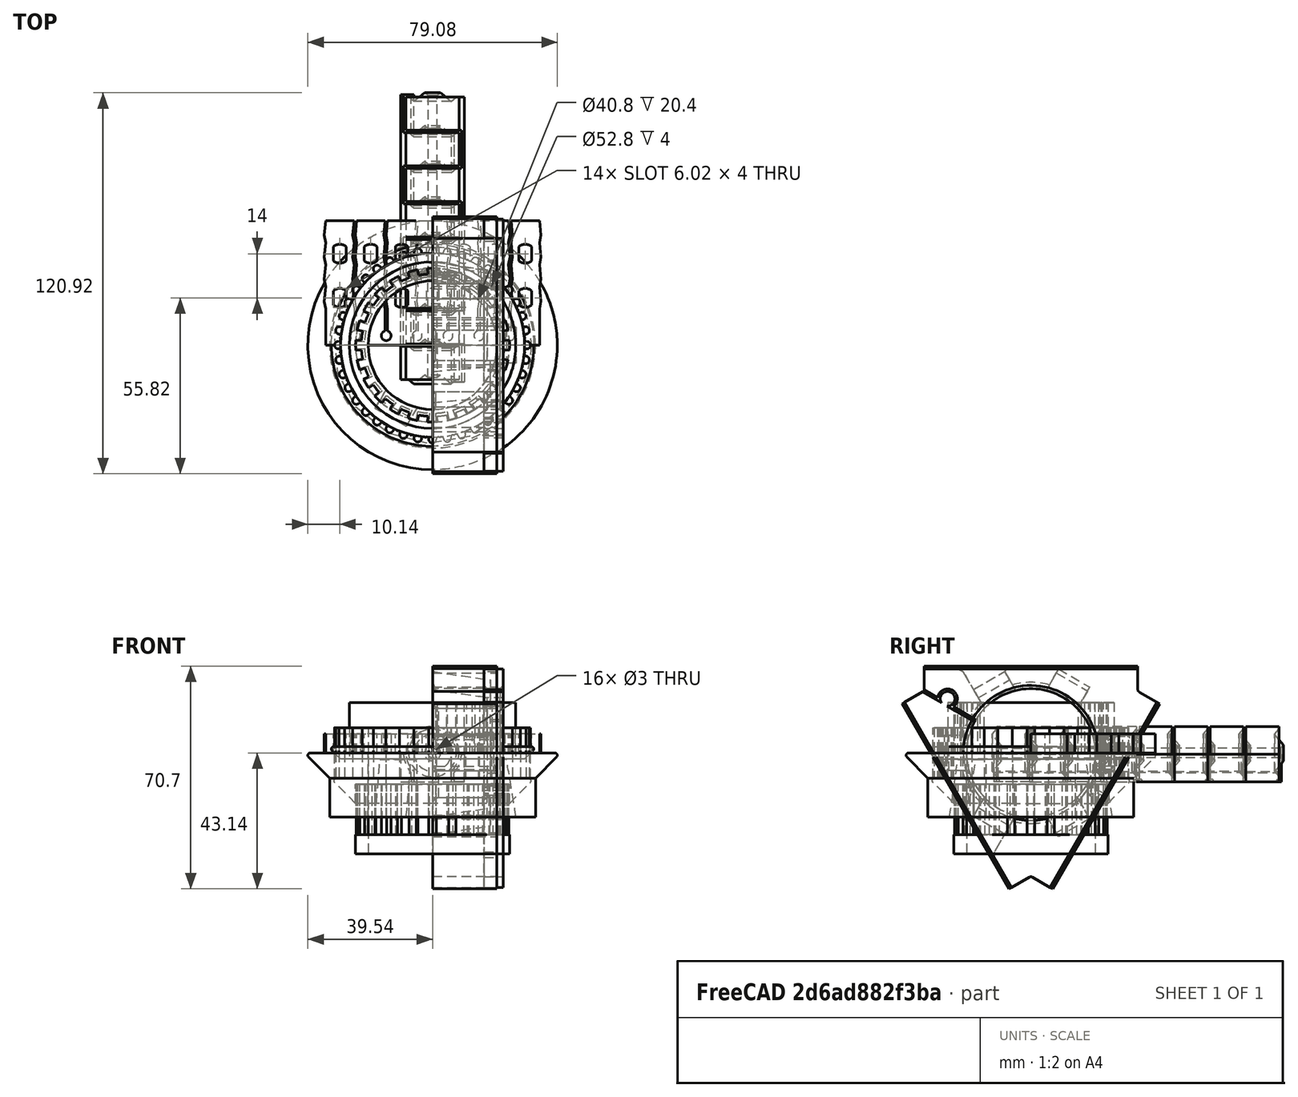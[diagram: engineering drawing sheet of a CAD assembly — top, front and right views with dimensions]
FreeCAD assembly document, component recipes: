
FREECAD ASSEMBLY — COMPONENT RECIPES ("BaseHingeModel_ver1.2_Base")

This assembly document has 10 components, labeled P0..P9 below (a component is one placed body or linked part). 10 of them carry a construction recipe — the FreeCAD feature program that regenerates the part from scratch, quoted from this document or its linked companion documents; the rest are supplied as boundary geometry only. No exploded tour is included for this assembly.
COMPONENT P0 — recipe-attached ("BeamFixatoPart", modeled in this document).
Construction recipe (the document's own serialized feature program — sketch geometry with constraints, then the solid features built on it; lengths are millimeters unless a unit is written):

FEATURE [Sketcher::SketchObject] Sketch022  label="FixatorBodySketch"
  FullyConstrained = false
  MapMode = 5
  Support = -> [XY_Plane005]
  expr: Constraints[143] = Spreadsheet.mmCellWall
  expr: Constraints[144] = Spreadsheet.mmCellWall
  expr: Constraints[145] = Spreadsheet.mmCellWall
  expr: Constraints[146] = Spreadsheet.mmCellWidth
  expr: Constraints[147] = Spreadsheet.mmCellWidth
  expr: Constraints[148] = Spreadsheet.mmCellWidth
  expr: Constraints[169] = Spreadsheet.mmCommonBaseLenght
  expr: Constraints[170] = Spreadsheet.mmToothStep
  expr: Constraints[171] = Spreadsheet.mmToothStep
  expr: Constraints[172] = Spreadsheet.mmToothStep
  expr: Constraints[173] = Spreadsheet.mmToothStep
  expr: Constraints[174] = Spreadsheet.mmToothStep
  expr: Constraints[183] = Spreadsheet.mmCellWall * 3
  expr: Constraints[184] = Spreadsheet.mmCellWall * 3
  expr: Constraints[185] = Spreadsheet.mmCellWall * 3
  expr: Constraints[186] = Spreadsheet.mmCellWall * 3
  expr: Constraints[425] = Spreadsheet.mmFirstCircleArcToBase
  expr: Constraints[435] = Spreadsheet.mmCellWall / 2
  expr: Constraints[464] = Spreadsheet.mmCellWidth + Spreadsheet.mmCellWall
  expr: Constraints[5] = Spreadsheet.mmBaseWidth
  expr: Constraints[6] = Spreadsheet.mmBaseEnd
  sketch-geometry (155):
    g0: LineSegment StartX=-33.9 StartY=0 StartZ=0 EndX=-33.9 EndY=39.5 EndZ=0
    g1: LineSegment StartX=-33.9 StartY=39.5 StartZ=0 EndX=33.9 EndY=39.5 EndZ=0
    g2: LineSegment StartX=33.9 StartY=39.5 StartZ=0 EndX=33.9 EndY=0 EndZ=0
    g3: LineSegment StartX=-73.1099 StartY=25.5 StartZ=0 EndX=65.6354 EndY=25.5 EndZ=0
    g4: LineSegment StartX=-33.9 StartY=0 StartZ=0 EndX=-33.9 EndY=11.5 EndZ=0
    g5: LineSegment StartX=-33.9 StartY=11.5 StartZ=0 EndX=-34.3 EndY=13.9 EndZ=0
    g6: LineSegment StartX=-34.3 StartY=13.9 StartZ=0 EndX=-33.9 EndY=18.5 EndZ=0
    g7: LineSegment StartX=-33.9 StartY=18.5 StartZ=0 EndX=-34.3 EndY=20.9 EndZ=0
    g8: LineSegment StartX=-34.3 StartY=20.9 StartZ=0 EndX=-33.9 EndY=25.5 EndZ=0
    g9: LineSegment StartX=-33.9 StartY=25.5 StartZ=0 EndX=-34.3 EndY=27.9 EndZ=0
    g10: LineSegment StartX=-34.3 StartY=27.9 StartZ=0 EndX=-33.9 EndY=32.5 EndZ=0
    g11: LineSegment StartX=-33.9 StartY=32.5 StartZ=0 EndX=-34.3 EndY=34.9 EndZ=0
    g12: LineSegment StartX=-34.3 StartY=34.9 StartZ=0 EndX=-33.9 EndY=39.5 EndZ=0
    g13: LineSegment StartX=-33.9 StartY=39.5 StartZ=0 EndX=-24.9 EndY=39.5 EndZ=0
    g14: LineSegment StartX=-24.9 StartY=39.5 StartZ=0 EndX=-25.3 EndY=34.9 EndZ=0
    g15: LineSegment StartX=-25.3 StartY=34.9 StartZ=0 EndX=-24.9 EndY=32.5 EndZ=0
    g16: LineSegment StartX=-24.9 StartY=32.5 StartZ=0 EndX=-25.3 EndY=27.9 EndZ=0
    g17: LineSegment StartX=-25.3 StartY=27.9 StartZ=0 EndX=-24.9 EndY=25.5 EndZ=0
    g18: LineSegment StartX=-24.9 StartY=25.5 StartZ=0 EndX=-25.3 EndY=20.9 EndZ=0
    g19: LineSegment StartX=-25.3 StartY=20.9 StartZ=0 EndX=-24.9 EndY=18.5 EndZ=0
    g20: LineSegment StartX=-24.9 StartY=18.5 StartZ=0 EndX=-25.3 EndY=13.9 EndZ=0
    g21: LineSegment StartX=-25.3 StartY=13.9 StartZ=0 EndX=-24.9 EndY=11.5 EndZ=0
    g22: LineSegment StartX=-24.9 StartY=11.5 StartZ=0 EndX=-24.9 EndY=4.5 EndZ=0
    g23: LineSegment StartX=-24.1 StartY=4.5 StartZ=0 EndX=-24.1 EndY=11.5 EndZ=0
    g24: LineSegment StartX=-24.1 StartY=11.5 StartZ=0 EndX=-24.5 EndY=13.9 EndZ=0
    g25: LineSegment StartX=-24.5 StartY=13.9 StartZ=0 EndX=-24.1 EndY=18.5 EndZ=0
    g26: LineSegment StartX=-24.1 StartY=18.5 StartZ=0 EndX=-24.5 EndY=20.9 EndZ=0
    g27: LineSegment StartX=-24.5 StartY=20.9 StartZ=0 EndX=-24.1 EndY=25.5 EndZ=0
    g28: LineSegment StartX=-24.1 StartY=25.5 StartZ=0 EndX=-24.5 EndY=27.9 EndZ=0
    g29: LineSegment StartX=-24.5 StartY=27.9 StartZ=0 EndX=-24.1 EndY=32.5 EndZ=0
    g30: LineSegment StartX=-24.1 StartY=32.5 StartZ=0 EndX=-24.5 EndY=34.9 EndZ=0
    g31: LineSegment StartX=-24.5 StartY=34.9 StartZ=0 EndX=-24.1 EndY=39.5 EndZ=0
    g32: LineSegment StartX=-24.1 StartY=39.5 StartZ=0 EndX=-15.1 EndY=39.5 EndZ=0
    g33: LineSegment StartX=-15.1 StartY=39.5 StartZ=0 EndX=-15.5 EndY=34.9 EndZ=0
    g34: LineSegment StartX=-15.5 StartY=34.9 StartZ=0 EndX=-15.1 EndY=32.5 EndZ=0
    g35: LineSegment StartX=-15.1 StartY=32.5 StartZ=0 EndX=-15.5 EndY=27.9 EndZ=0
    g36: LineSegment StartX=-15.5 StartY=27.9 StartZ=0 EndX=-15.1 EndY=25.5 EndZ=0
    g37: LineSegment StartX=-15.1 StartY=25.5 StartZ=0 EndX=-15.5 EndY=20.9 EndZ=0
    g38: LineSegment StartX=-15.5 StartY=20.9 StartZ=0 EndX=-15.1 EndY=18.5 EndZ=0
    g39: LineSegment StartX=-15.1 StartY=18.5 StartZ=0 EndX=-15.5 EndY=13.9 EndZ=0
    g40: LineSegment StartX=-15.5 StartY=13.9 StartZ=0 EndX=-15.1 EndY=11.5 EndZ=0
    g41: LineSegment StartX=-15.1 StartY=11.5 StartZ=0 EndX=-15.1 EndY=4.5 EndZ=0
    g42: LineSegment StartX=-14.3 StartY=4.5 StartZ=0 EndX=-14.3 EndY=11.5 EndZ=0
    g43: LineSegment StartX=-14.3 StartY=11.5 StartZ=0 EndX=-14.7 EndY=13.9 EndZ=0
    g44: LineSegment StartX=-14.7 StartY=13.9 StartZ=0 EndX=-14.3 EndY=18.5 EndZ=0
    g45: LineSegment StartX=-14.3 StartY=18.5 StartZ=0 EndX=-14.7 EndY=20.9 EndZ=0
    g46: LineSegment StartX=-14.7 StartY=20.9 StartZ=0 EndX=-14.3 EndY=25.5 EndZ=0
    g47: LineSegment StartX=-14.3 StartY=25.5 StartZ=0 EndX=-14.7 EndY=27.9 EndZ=0
    g48: LineSegment StartX=-14.7 StartY=27.9 StartZ=0 EndX=-14.3 EndY=32.5 EndZ=0
    g49: LineSegment StartX=-14.3 StartY=32.5 StartZ=0 EndX=-14.7 EndY=34.9 EndZ=0
    g50: LineSegment StartX=-14.7 StartY=34.9 StartZ=0 EndX=-14.3 EndY=39.5 EndZ=0
    g51: LineSegment StartX=-14.3 StartY=39.5 StartZ=0 EndX=-5.3 EndY=39.5 EndZ=0
    g52: LineSegment StartX=-5.3 StartY=39.5 StartZ=0 EndX=-5.7 EndY=34.9 EndZ=0
    g53: LineSegment StartX=-5.7 StartY=34.9 StartZ=0 EndX=-5.3 EndY=32.5 EndZ=0
    g54: LineSegment StartX=-5.3 StartY=32.5 StartZ=0 EndX=-5.7 EndY=27.9 EndZ=0
    g55: LineSegment StartX=-5.7 StartY=27.9 StartZ=0 EndX=-5.3 EndY=25.5 EndZ=0
    g56: LineSegment StartX=-5.3 StartY=25.5 StartZ=0 EndX=-5.7 EndY=20.9 EndZ=0
    g57: LineSegment StartX=-5.7 StartY=20.9 StartZ=0 EndX=-5.3 EndY=18.5 EndZ=0
    g58: LineSegment StartX=-5.3 StartY=18.5 StartZ=0 EndX=-5.7 EndY=13.9 EndZ=0
    g59: LineSegment StartX=-5.7 StartY=13.9 StartZ=0 EndX=-5.3 EndY=11.5 EndZ=0
    g60: LineSegment StartX=-5.3 StartY=11.5 StartZ=0 EndX=-5.3 EndY=4.5 EndZ=0
    g61: LineSegment StartX=-4.5 StartY=4.5 StartZ=0 EndX=-4.5 EndY=11.5 EndZ=0
    g62: LineSegment StartX=-4.5 StartY=11.5 StartZ=0 EndX=-4.9 EndY=13.9 EndZ=0
    g63: LineSegment StartX=-4.9 StartY=13.9 StartZ=0 EndX=-4.5 EndY=18.5 EndZ=0
    g64: LineSegment StartX=-4.5 StartY=18.5 StartZ=0 EndX=-4.9 EndY=20.9 EndZ=0
    g65: LineSegment StartX=-4.9 StartY=20.9 StartZ=0 EndX=-4.5 EndY=25.5 EndZ=0
    g66: LineSegment StartX=-4.5 StartY=25.5 StartZ=0 EndX=-4.9 EndY=27.9 EndZ=0
    g67: LineSegment StartX=-4.9 StartY=27.9 StartZ=0 EndX=-4.5 EndY=32.5 EndZ=0
    g68: LineSegment StartX=-4.5 StartY=32.5 StartZ=0 EndX=-4.9 EndY=34.9 EndZ=0
    g69: LineSegment StartX=-4.9 StartY=34.9 StartZ=0 EndX=-4.5 EndY=39.5 EndZ=0
    g70: LineSegment StartX=-4.5 StartY=39.5 StartZ=0 EndX=4.5 EndY=39.5 EndZ=0
    g71: LineSegment StartX=4.5 StartY=39.5 StartZ=0 EndX=4.9 EndY=34.9 EndZ=0
    g72: LineSegment StartX=4.9 StartY=34.9 StartZ=0 EndX=4.5 EndY=32.5 EndZ=0
    g73: LineSegment StartX=4.5 StartY=32.5 StartZ=0 EndX=4.9 EndY=27.9 EndZ=0
    g74: LineSegment StartX=4.9 StartY=27.9 StartZ=0 EndX=4.5 EndY=25.5 EndZ=0
    g75: LineSegment StartX=4.5 StartY=25.5 StartZ=0 EndX=4.9 EndY=20.9 EndZ=0
    g76: LineSegment StartX=4.9 StartY=20.9 StartZ=0 EndX=4.5 EndY=18.5 EndZ=0
    g77: LineSegment StartX=4.5 StartY=18.5 StartZ=0 EndX=4.9 EndY=13.9 EndZ=0
    g78: LineSegment StartX=4.9 StartY=13.9 StartZ=0 EndX=4.5 EndY=11.5 EndZ=0
    g79: LineSegment StartX=4.5 StartY=11.5 StartZ=0 EndX=4.5 EndY=4.5 EndZ=0
    g80: LineSegment StartX=5.3 StartY=4.5 StartZ=0 EndX=5.3 EndY=11.5 EndZ=0
    g81: LineSegment StartX=5.3 StartY=11.5 StartZ=0 EndX=5.7 EndY=13.9 EndZ=0
    g82: LineSegment StartX=5.7 StartY=13.9 StartZ=0 EndX=5.3 EndY=18.5 EndZ=0
    g83: LineSegment StartX=5.3 StartY=18.5 StartZ=0 EndX=5.7 EndY=20.9 EndZ=0
    g84: LineSegment StartX=5.7 StartY=20.9 StartZ=0 EndX=5.3 EndY=25.5 EndZ=0
    g85: LineSegment StartX=5.3 StartY=25.5 StartZ=0 EndX=5.7 EndY=27.9 EndZ=0
    g86: LineSegment StartX=5.7 StartY=27.9 StartZ=0 EndX=5.3 EndY=32.5 EndZ=0
    g87: LineSegment StartX=5.3 StartY=32.5 StartZ=0 EndX=5.7 EndY=34.9 EndZ=0
    g88: LineSegment StartX=5.7 StartY=34.9 StartZ=0 EndX=5.3 EndY=39.5 EndZ=0
    g89: LineSegment StartX=5.3 StartY=39.5 StartZ=0 EndX=14.3 EndY=39.5 EndZ=0
    g90: LineSegment StartX=14.3 StartY=39.5 StartZ=0 EndX=14.7 EndY=34.9 EndZ=0
    g91: LineSegment StartX=14.7 StartY=34.9 StartZ=0 EndX=14.3 EndY=32.5 EndZ=0
    g92: LineSegment StartX=14.3 StartY=32.5 StartZ=0 EndX=14.7 EndY=27.9 EndZ=0
    g93: LineSegment StartX=14.7 StartY=27.9 StartZ=0 EndX=14.3 EndY=25.5 EndZ=0
    g94: LineSegment StartX=14.3 StartY=25.5 StartZ=0 EndX=14.7 EndY=20.9 EndZ=0
    g95: LineSegment StartX=14.7 StartY=20.9 StartZ=0 EndX=14.3 EndY=18.5 EndZ=0
    g96: LineSegment StartX=14.3 StartY=18.5 StartZ=0 EndX=14.7 EndY=13.9 EndZ=0
    g97: LineSegment StartX=14.7 StartY=13.9 StartZ=0 EndX=14.3 EndY=11.5 EndZ=0
    g98: LineSegment StartX=14.3 StartY=11.5 StartZ=0 EndX=14.3 EndY=4.5 EndZ=0
    g99: LineSegment StartX=15.1 StartY=4.5 StartZ=0 EndX=15.1 EndY=11.5 EndZ=0
    g100: LineSegment StartX=15.1 StartY=11.5 StartZ=0 EndX=15.5 EndY=13.9 EndZ=0
    g101: LineSegment StartX=15.5 StartY=13.9 StartZ=0 EndX=15.1 EndY=18.5 EndZ=0
    g102: LineSegment StartX=15.1 StartY=18.5 StartZ=0 EndX=15.5 EndY=20.9 EndZ=0
    g103: LineSegment StartX=15.5 StartY=20.9 StartZ=0 EndX=15.1 EndY=25.5 EndZ=0
    g104: LineSegment StartX=15.1 StartY=25.5 StartZ=0 EndX=15.5 EndY=27.9 EndZ=0
    g105: LineSegment StartX=15.5 StartY=27.9 StartZ=0 EndX=15.1 EndY=32.5 EndZ=0
    g106: LineSegment StartX=15.1 StartY=32.5 StartZ=0 EndX=15.5 EndY=34.9 EndZ=0
    g107: LineSegment StartX=15.5 StartY=34.9 StartZ=0 EndX=15.1 EndY=39.5 EndZ=0
    g108: LineSegment StartX=15.1 StartY=39.5 StartZ=0 EndX=24.1 EndY=39.5 EndZ=0
    g109: LineSegment StartX=24.1 StartY=39.5 StartZ=0 EndX=24.5 EndY=34.9 EndZ=0
    g110: LineSegment StartX=24.5 StartY=34.9 StartZ=0 EndX=24.1 EndY=32.5 EndZ=0
    g111: LineSegment StartX=24.1 StartY=32.5 StartZ=0 EndX=24.5 EndY=27.9 EndZ=0
    g112: LineSegment StartX=24.5 StartY=27.9 StartZ=0 EndX=24.1 EndY=25.5 EndZ=0
    g113: LineSegment StartX=24.1 StartY=25.5 StartZ=0 EndX=24.5 EndY=20.9 EndZ=0
    g114: LineSegment StartX=24.5 StartY=20.9 StartZ=0 EndX=24.1 EndY=18.5 EndZ=0
    g115: LineSegment StartX=24.1 StartY=18.5 StartZ=0 EndX=24.5 EndY=13.9 EndZ=0
    g116: LineSegment StartX=24.5 StartY=13.9 StartZ=0 EndX=24.1 EndY=11.5 EndZ=0
    g117: LineSegment StartX=24.1 StartY=11.5 StartZ=0 EndX=24.1 EndY=4.5 EndZ=0
    g118: LineSegment StartX=24.9 StartY=4.5 StartZ=0 EndX=24.9 EndY=11.5 EndZ=0
    g119: LineSegment StartX=24.9 StartY=11.5 StartZ=0 EndX=25.3 EndY=13.9 EndZ=0
    g120: LineSegment StartX=25.3 StartY=13.9 StartZ=0 EndX=24.9 EndY=18.5 EndZ=0
    g121: LineSegment StartX=24.9 StartY=18.5 StartZ=0 EndX=25.3 EndY=20.9 EndZ=0
    g122: LineSegment StartX=25.3 StartY=20.9 StartZ=0 EndX=24.9 EndY=25.5 EndZ=0
    g123: LineSegment StartX=24.9 StartY=25.5 StartZ=0 EndX=25.3 EndY=27.9 EndZ=0
    g124: LineSegment StartX=25.3 StartY=27.9 StartZ=0 EndX=24.9 EndY=32.5 EndZ=0
    g125: LineSegment StartX=24.9 StartY=32.5 StartZ=0 EndX=25.3 EndY=34.9 EndZ=0
    g126: LineSegment StartX=25.3 StartY=34.9 StartZ=0 EndX=24.9 EndY=39.5 EndZ=0
    g127: LineSegment StartX=24.9 StartY=39.5 StartZ=0 EndX=33.9 EndY=39.5 EndZ=0
    g128: LineSegment StartX=33.9 StartY=39.5 StartZ=0 EndX=34.3 EndY=34.9 EndZ=0
    g129: LineSegment StartX=34.3 StartY=34.9 StartZ=0 EndX=33.9 EndY=32.5 EndZ=0
    g130: LineSegment StartX=33.9 StartY=32.5 StartZ=0 EndX=34.3 EndY=27.9 EndZ=0
    g131: LineSegment StartX=34.3 StartY=27.9 StartZ=0 EndX=33.9 EndY=25.5 EndZ=0
    g132: LineSegment StartX=33.9 StartY=25.5 StartZ=0 EndX=34.3 EndY=20.9 EndZ=0
    g133: LineSegment StartX=34.3 StartY=20.9 StartZ=0 EndX=33.9 EndY=18.5 EndZ=0
    g134: LineSegment StartX=33.9 StartY=18.5 StartZ=0 EndX=34.3 EndY=13.9 EndZ=0
    g135: LineSegment StartX=34.3 StartY=13.9 StartZ=0 EndX=33.9 EndY=11.5 EndZ=0
    g136: LineSegment StartX=33.9 StartY=11.5 StartZ=0 EndX=33.9 EndY=0 EndZ=0
    g137: LineSegment StartX=33.9 StartY=0 StartZ=0 EndX=-33.9 EndY=0 EndZ=0
    g138: LineSegment StartX=-73.1099 StartY=18.5 StartZ=0 EndX=65.6354 EndY=18.5 EndZ=0
    g139: LineSegment StartX=-73.1099 StartY=34.9 StartZ=0 EndX=65.6354 EndY=34.9 EndZ=0
    g140: LineSegment StartX=-73.1099 StartY=32.5 StartZ=0 EndX=65.6354 EndY=32.5 EndZ=0
    g141: LineSegment StartX=-73.1099 StartY=27.9 StartZ=0 EndX=65.6354 EndY=27.9 EndZ=0
    g142: LineSegment StartX=-73.1099 StartY=20.9 StartZ=0 EndX=65.6354 EndY=20.9 EndZ=0
    g143: LineSegment StartX=-73.1099 StartY=11.5 StartZ=0 EndX=65.6354 EndY=11.5 EndZ=0
    g144: LineSegment StartX=-34.3 StartY=8.59208 StartZ=0 EndX=-34.3 EndY=49.4346 EndZ=0
    g145: LineSegment StartX=-73.1099 StartY=13.9 StartZ=0 EndX=65.6354 EndY=13.9 EndZ=0
    g146: LineSegment StartX=-33.9 StartY=0 StartZ=0 EndX=33.9 EndY=0 EndZ=0
    g147: LineSegment StartX=-73.1099 StartY=4.5 StartZ=0 EndX=65.6354 EndY=4.5 EndZ=0
    g148: ArcOfCircle CenterX=-24.5 CenterY=3 CenterZ=0 NormalX=0 NormalY=0 NormalZ=1 AngleXU=0 Radius=1.55242 StartAngle=1.8314 EndAngle=7.59338
    g149: ArcOfCircle CenterX=-14.7 CenterY=3 CenterZ=0 NormalX=0 NormalY=0 NormalZ=1 AngleXU=0 Radius=1.55242 StartAngle=1.8314 EndAngle=7.59338
    g150: ArcOfCircle CenterX=-4.9 CenterY=3 CenterZ=0 NormalX=0 NormalY=0 NormalZ=1 AngleXU=0 Radius=1.55242 StartAngle=1.8314 EndAngle=7.59338
    g151: ArcOfCircle CenterX=4.9 CenterY=3 CenterZ=0 NormalX=0 NormalY=0 NormalZ=1 AngleXU=0 Radius=1.55242 StartAngle=1.8314 EndAngle=7.59338
    g152: ArcOfCircle CenterX=14.7 CenterY=3 CenterZ=0 NormalX=0 NormalY=0 NormalZ=1 AngleXU=0 Radius=1.55242 StartAngle=1.8314 EndAngle=7.59338
    g153: ArcOfCircle CenterX=24.5 CenterY=3 CenterZ=0 NormalX=0 NormalY=0 NormalZ=1 AngleXU=0 Radius=1.55242 StartAngle=1.8314 EndAngle=7.59338
    g154: LineSegment StartX=-73.1099 StartY=3 StartZ=0 EndX=65.6354 EndY=3 EndZ=0
  constraints (469):
    c: Coincident(g0,g1)
    c: Coincident(g1,g2)
    c: Horizontal(g3)
    c: Symmetric(g0,g2,g-2)
    c: Symmetric(g1,g0,g-2)
    c: DistanceX(g0,g2) = 67.8
    c: DistanceX(g0,g1) = 67.8
    c: Coincident(g4,g5)
    c: Coincident(g5,g6)
    c: Coincident(g6,g7)
    c: Coincident(g7,g8)
    c: Coincident(g8,g9)
    c: Coincident(g9,g10)
    c: Coincident(g10,g11)
    c: Coincident(g11,g12)
    c: Coincident(g12,g13)
    c: Horizontal(g13)
    c: Coincident(g13,g14)
    c: Coincident(g14,g15)
    c: Coincident(g15,g16)
    c: Coincident(g16,g17)
    c: Coincident(g17,g18)
    c: Coincident(g18,g19)
    c: Coincident(g19,g20)
    c: Coincident(g20,g21)
    c: Coincident(g21,g22)
    c: Coincident(g23,g24)
    c: Coincident(g24,g25)
    c: Coincident(g25,g26)
    c: Coincident(g26,g27)
    c: Coincident(g27,g28)
    c: Coincident(g28,g29)
    c: Coincident(g29,g30)
    c: Coincident(g30,g31)
    c: Coincident(g31,g32)
    c: Horizontal(g32)
    c: Coincident(g32,g33)
    c: Coincident(g33,g34)
    c: Coincident(g34,g35)
    c: Coincident(g35,g36)
    c: Coincident(g36,g37)
    c: Coincident(g37,g38)
    c: Coincident(g38,g39)
    c: Coincident(g39,g40)
    c: Coincident(g40,g41)
    c: Coincident(g42,g43)
    c: Coincident(g43,g44)
    c: Coincident(g44,g45)
    c: Coincident(g45,g46)
    c: Coincident(g46,g47)
    c: Coincident(g47,g48)
    c: Coincident(g48,g49)
    c: Coincident(g49,g50)
    c: Coincident(g50,g51)
    c: Coincident(g51,g52)
    c: Coincident(g52,g53)
    c: Coincident(g53,g54)
    c: Coincident(g54,g55)
    c: Coincident(g55,g56)
    c: Coincident(g56,g57)
    c: Coincident(g57,g58)
    c: Coincident(g58,g59)
    c: Coincident(g59,g60)
    c: Coincident(g61,g62)
    c: Coincident(g62,g63)
    c: Coincident(g63,g64)
    c: Coincident(g64,g65)
    c: Coincident(g65,g66)
    c: Coincident(g66,g67)
    c: Coincident(g67,g68)
    c: Coincident(g68,g69)
    c: Coincident(g69,g70)
    c: Coincident(g70,g71)
    c: Coincident(g71,g72)
    c: Coincident(g72,g73)
    c: Coincident(g73,g74)
    c: Coincident(g74,g75)
    c: Coincident(g75,g76)
    c: Coincident(g76,g77)
    c: Coincident(g77,g78)
    c: Coincident(g78,g79)
    c: Coincident(g80,g81)
    c: Coincident(g81,g82)
    c: Coincident(g82,g83)
    c: Coincident(g83,g84)
    c: Coincident(g84,g85)
    c: Coincident(g85,g86)
    c: Coincident(g86,g87)
    c: Coincident(g87,g88)
    c: Coincident(g88,g89)
    c: Horizontal(g89)
    c: Coincident(g89,g90)
    c: Coincident(g90,g91)
    c: Coincident(g91,g92)
    c: Coincident(g92,g93)
    c: Coincident(g93,g94)
    c: Coincident(g94,g95)
    c: Coincident(g95,g96)
    c: Coincident(g96,g97)
    c: Coincident(g97,g98)
    c: Coincident(g99,g100)
    c: Coincident(g100,g101)
    c: Coincident(g101,g102)
    c: Coincident(g102,g103)
    c: Coincident(g103,g104)
    c: Coincident(g104,g105)
    c: Coincident(g105,g106)
    c: Coincident(g106,g107)
    c: Coincident(g107,g108)
    c: Coincident(g108,g109)
    c: Coincident(g109,g110)
    c: Coincident(g110,g111)
    c: Coincident(g111,g112)
    c: Coincident(g112,g113)
    c: Coincident(g113,g114)
    c: Coincident(g114,g115)
    c: Coincident(g115,g116)
    c: Coincident(g116,g117)
    c: Coincident(g118,g119)
    c: Coincident(g119,g120)
    c: Coincident(g120,g121)
    c: Coincident(g121,g122)
    c: Coincident(g122,g123)
    c: Coincident(g123,g124)
    c: Coincident(g124,g125)
    c: Coincident(g125,g126)
    c: Coincident(g126,g127)
    c: Coincident(g127,g128)
    c: Coincident(g128,g129)
    c: Coincident(g129,g130)
    c: Coincident(g130,g131)
    c: Coincident(g131,g132)
    c: Coincident(g132,g133)
    c: Coincident(g133,g134)
    c: Coincident(g134,g135)
    c: Coincident(g135,g136)
    c: Symmetric(g69,g70,g-2)
    c: Symmetric(g51,g88,g-2)
    c: Symmetric(g50,g89,g-2)
    c: Symmetric(g32,g107,g-2)
    c: Symmetric(g31,g108,g-2)
    c: Symmetric(g13,g126,g-2)
    c: Symmetric(g12,g127,g-2)
    c: DistanceX(g13,g31) = 0.8
    c: DistanceX(g32,g50) = 0.8
    c: DistanceX(g51,g69) = 0.8
    c: DistanceX(g13,g13) = 9
    c: DistanceX(g32,g32) = 9
    c: DistanceX(g51,g51) = 9
    c: Horizontal(g139)
    c: Horizontal(g140)
    c: Horizontal(g141)
    c: Horizontal(g142)
    c: Horizontal(g143)
    c: Vertical(g8,g6)
    c: Vertical(g6,g4)
    c: Vertical(g144)
    c: Horizontal(g145)
    c: Coincident(g146,g0)
    c: Coincident(g146,g2)
    c: Coincident(g0,g137)
    c: Coincident(g2,g137)
    c: Horizontal(g147)
    c: PointOnObject(g11,g139)
    c: PointOnObject(g11,g144)
    c: PointOnObject(g10,g140)
    c: PointOnObject(g9,g144)
    c: PointOnObject(g7,g142)
    c: Horizontal(g138)
    c: DistanceY(g137,g147) = 4.5
    c: DistanceY(g147,g143) = 7
    c: DistanceY(g143,g138) = 7
    c: DistanceY(g138,g3) = 7
    c: DistanceY(g3,g140) = 7
    c: DistanceY(g140,g0) = 7
    c: Vertical(g139,g140)
    c: Vertical(g140,g141)
    c: Vertical(g141,g3)
    c: Vertical(g3,g142)
    c: Vertical(g142,g138)
    c: Vertical(g138,g145)
    c: Vertical(g145,g143)
    c: Vertical(g143,g147)
    c: DistanceY(g143,g145) = 2.4
    c: DistanceY(g138,g142) = 2.4
    c: DistanceY(g3,g141) = 2.4
    c: DistanceY(g140,g139) = 2.4
    c: Parallel(g12,g14)
    c: Parallel(g11,g15)
    c: PointOnObject(g14,g139)
    c: PointOnObject(g30,g139)
    c: PointOnObject(g15,g140)
    c: PointOnObject(g29,g140)
    c: Parallel(g14,g31)
    c: PointOnObject(g16,g141)
    c: PointOnObject(g28,g141)
    c: PointOnObject(g17,g3)
    c: PointOnObject(g27,g3)
    c: PointOnObject(g18,g142)
    c: PointOnObject(g26,g142)
    c: PointOnObject(g19,g138)
    c: PointOnObject(g25,g138)
    c: PointOnObject(g20,g145)
    c: PointOnObject(g24,g145)
    c: PointOnObject(g21,g143)
    c: PointOnObject(g23,g143)
    c: PointOnObject(g22,g147)
    c: PointOnObject(g23,g147)
    c: PointOnObject(g33,g139)
    c: PointOnObject(g49,g139)
    c: PointOnObject(g52,g139)
    c: PointOnObject(g71,g139)
    c: PointOnObject(g87,g139)
    c: PointOnObject(g90,g139)
    c: PointOnObject(g106,g139)
    c: PointOnObject(g109,g139)
    c: PointOnObject(g125,g139)
    c: PointOnObject(g128,g139)
    c: PointOnObject(g34,g140)
    c: PointOnObject(g48,g140)
    c: PointOnObject(g53,g140)
    c: PointOnObject(g67,g140)
    c: PointOnObject(g72,g140)
    c: PointOnObject(g86,g140)
    c: PointOnObject(g91,g140)
    c: PointOnObject(g105,g140)
    c: PointOnObject(g110,g140)
    c: PointOnObject(g124,g140)
    c: PointOnObject(g129,g140)
    c: Parallel(g33,g50)
    c: Parallel(g52,g69)
    c: Parallel(g71,g88)
    c: Parallel(g71,g90)
    c: Parallel(g90,g107)
    c: Parallel(g71,g109)
    c: Parallel(g109,g126)
    c: Parallel(g126,g128)
    c: Symmetric(g71,g68,g-2)
    c: Symmetric(g72,g67,g-2)
    c: Vertical(g139,g140)
    c: Vertical(g140,g141)
    c: Vertical(g141,g3)
    c: Vertical(g3,g142)
    c: Vertical(g142,g138)
    c: Vertical(g138,g145)
    c: Vertical(g145,g143)
    c: Vertical(g143,g147)
    c: Parallel(g34,g49)
    c: Parallel(g49,g53)
    c: Parallel(g53,g68)
    c: Parallel(g35,g48)
    c: Parallel(g48,g54)
    c: Parallel(g54,g67)
    c: PointOnObject(g35,g141)
    c: PointOnObject(g47,g141)
    c: PointOnObject(g54,g141)
    c: PointOnObject(g66,g141)
    c: PointOnObject(g85,g141)
    c: PointOnObject(g92,g141)
    c: PointOnObject(g104,g141)
    c: PointOnObject(g111,g141)
    c: PointOnObject(g123,g141)
    c: PointOnObject(g130,g141)
    c: Symmetric(g66,g73,g-2)
    c: Symmetric(g65,g74,g-2)
    c: PointOnObject(g36,g3)
    c: PointOnObject(g46,g3)
    c: PointOnObject(g55,g3)
    c: PointOnObject(g65,g3)
    c: Parallel(g36,g47)
    c: Parallel(g47,g55)
    c: Parallel(g55,g66)
    c: Symmetric(g64,g75,g-2)
    c: Symmetric(g79,g61,g-2)
    c: Symmetric(g61,g78,g-2)
    c: Symmetric(g62,g77,g-2)
    c: Symmetric(g63,g76,g-2)
    c: Parallel(g37,g46)
    c: Parallel(g46,g56)
    c: Parallel(g56,g65)
    c: PointOnObject(g37,g142)
    c: PointOnObject(g45,g142)
    c: PointOnObject(g56,g142)
    c: PointOnObject(g64,g142)
    c: PointOnObject(g38,g138)
    c: PointOnObject(g44,g138)
    c: PointOnObject(g57,g138)
    c: PointOnObject(g63,g138)
    c: Parallel(g38,g45)
    c: Parallel(g45,g57)
    c: Parallel(g57,g64)
    c: PointOnObject(g39,g145)
    c: PointOnObject(g43,g145)
    c: PointOnObject(g58,g145)
    c: PointOnObject(g62,g145)
    c: Parallel(g39,g44)
    c: Parallel(g44,g58)
    c: Parallel(g58,g63)
    c: Parallel(g40,g43)
    c: Parallel(g43,g59)
    c: Parallel(g59,g62)
    c: PointOnObject(g40,g143)
    c: PointOnObject(g42,g143)
    c: PointOnObject(g59,g143)
    c: PointOnObject(g61,g143)
    c: PointOnObject(g41,g147)
    c: PointOnObject(g42,g147)
    c: PointOnObject(g60,g147)
    c: PointOnObject(g61,g147)
    c: Parallel(g41,g42)
    c: Parallel(g42,g60)
    c: Parallel(g60,g61)
    c: PointOnObject(g80,g147)
    c: PointOnObject(g98,g147)
    c: PointOnObject(g99,g147)
    c: PointOnObject(g117,g147)
    c: PointOnObject(g118,g147)
    c: PointOnObject(g80,g143)
    c: PointOnObject(g97,g143)
    c: PointOnObject(g99,g143)
    c: PointOnObject(g116,g143)
    c: PointOnObject(g118,g143)
    c: PointOnObject(g135,g143)
    c: Parallel(g79,g80)
    c: Parallel(g80,g98)
    c: Parallel(g98,g99)
    c: Parallel(g99,g117)
    c: Parallel(g117,g118)
    c: Parallel(g118,g136)
    c: Parallel(g72,g87)
    c: Parallel(g87,g91)
    c: Parallel(g91,g106)
    c: Parallel(g106,g110)
    c: Parallel(g110,g125)
    c: Parallel(g125,g129)
    c: Parallel(g73,g86)
    c: Parallel(g86,g92)
    c: Parallel(g92,g105)
    c: Parallel(g105,g111)
    c: Parallel(g111,g124)
    c: Parallel(g124,g130)
    c: PointOnObject(g84,g3)
    c: PointOnObject(g93,g3)
    c: PointOnObject(g103,g3)
    c: PointOnObject(g112,g3)
    c: PointOnObject(g122,g3)
    c: PointOnObject(g131,g3)
    c: Parallel(g74,g85)
    c: Parallel(g85,g93)
    c: Parallel(g93,g104)
    c: Parallel(g104,g112)
    c: Parallel(g112,g123)
    c: Parallel(g123,g131)
    c: PointOnObject(g83,g142)
    c: PointOnObject(g94,g142)
    c: PointOnObject(g102,g142)
    c: PointOnObject(g113,g142)
    c: PointOnObject(g121,g142)
    c: PointOnObject(g132,g142)
    c: Parallel(g75,g84)
    c: Parallel(g84,g94)
    c: Parallel(g94,g103)
    c: Parallel(g103,g113)
    c: Parallel(g113,g122)
    c: Parallel(g122,g132)
    c: PointOnObject(g82,g138)
    c: PointOnObject(g95,g138)
    c: PointOnObject(g101,g138)
    c: PointOnObject(g114,g138)
    c: PointOnObject(g120,g138)
    c: PointOnObject(g133,g138)
    c: PointOnObject(g81,g145)
    c: PointOnObject(g96,g145)
    c: PointOnObject(g100,g145)
    c: PointOnObject(g115,g145)
    c: PointOnObject(g119,g145)
    c: PointOnObject(g134,g145)
    c: Parallel(g76,g83)
    c: Parallel(g83,g95)
    c: Parallel(g95,g102)
    c: Parallel(g102,g114)
    c: Parallel(g114,g121)
    c: Parallel(g121,g133)
    c: Parallel(g77,g82)
    c: Parallel(g82,g96)
    c: Parallel(g96,g101)
    c: Parallel(g101,g115)
    c: Parallel(g115,g120)
    c: Parallel(g120,g134)
    c: Parallel(g78,g81)
    c: Parallel(g81,g97)
    c: Parallel(g97,g100)
    c: Parallel(g100,g116)
    c: Parallel(g116,g119)
    c: Parallel(g119,g135)
    c: DistanceY(g137,g-1) = 0
    c: PointOnObject(g148,g154)
    c: PointOnObject(g149,g154)
    c: PointOnObject(g150,g154)
    c: PointOnObject(g151,g154)
    c: PointOnObject(g152,g154)
    c: PointOnObject(g153,g154)
    c: PointOnObject(g22,g148)
    c: PointOnObject(g23,g148)
    c: PointOnObject(g41,g149)
    c: PointOnObject(g42,g149)
    c: PointOnObject(g60,g150)
    c: PointOnObject(g61,g150)
    c: PointOnObject(g79,g151)
    c: PointOnObject(g98,g152)
    c: PointOnObject(g99,g152)
    c: PointOnObject(g117,g153)
    c: PointOnObject(g118,g153)
    c: PointOnObject(g153,g147)
    c: PointOnObject(g153,g147)
    c: PointOnObject(g152,g147)
    c: PointOnObject(g152,g147)
    c: PointOnObject(g151,g147)
    c: PointOnObject(g151,g147)
    c: PointOnObject(g150,g147)
    c: PointOnObject(g150,g147)
    c: PointOnObject(g149,g147)
    c: PointOnObject(g149,g147)
    c: PointOnObject(g148,g147)
    c: PointOnObject(g148,g147)
    c: DistanceY(g154,g147) = 1.5
    c: Vertical(g147,g154)
    c: Vertical(g147,g154)
    c: Coincident(g136,g137)
    c: Coincident(g4,g137)
    c: Coincident(g0,g12)
    c: PointOnObject(g31,g1)
    c: PointOnObject(g50,g1)
    c: PointOnObject(g69,g1)
    c: PointOnObject(g6,g0)
    c: DistanceX(g144,g12) = 0.4
    c: PointOnObject(g9,g141)
    c: PointOnObject(g8,g3)
    c: PointOnObject(g7,g144)
    c: PointOnObject(g6,g138)
    c: PointOnObject(g5,g145)
    c: PointOnObject(g5,g144)
    c: PointOnObject(g4,g143)
    c: Parallel(g12,g33)
    c: Parallel(g12,g52)
    c: Parallel(g15,g30)
    c: Parallel(g11,g34)
    c: PointOnObject(g10,g0)
    c: Parallel(g16,g29)
    c: Parallel(g10,g16)
    c: Parallel(g10,g35)
    c: Parallel(g9,g17)
    c: Parallel(g17,g28)
    c: Parallel(g9,g36)
    c: Parallel(g18,g27)
    c: Parallel(g8,g18)
    c: Parallel(g8,g37)
    c: Parallel(g7,g19)
    c: Parallel(g19,g26)
    c: Parallel(g6,g20)
    c: Parallel(g20,g25)
    c: Parallel(g7,g38)
    c: Parallel(g6,g39)
    c: Symmetric(g150,g151,g-2)
    c: DistanceX(g150,g151) = 9.8
    c: Parallel(g23,g22)
    c: Parallel(g21,g24)
    c: Parallel(g5,g21)
    c: Parallel(g41,g23)
FEATURE [PartDesign::Pad] Pad  label="FixatorPadBody"
  Direction = (0,0,1)
  Length = 6
  Length2 = 10
  Profile = -> Sketch022
  ReferenceAxis = -> Sketch022 [N_Axis]
  Type = 0
  expr: Length = Spreadsheet.mmCellHight
FEATURE [Sketcher::SketchObject] Sketch  label="PiercesPocketSketch"
  AttachmentOffset = pos=(0,0,0) rot=(1,0,0;1.5708rad)
  FullyConstrained = true
  MapMode = 2
  Placement = pos=(0,0,0) rot=(0.707107,0.707107,0;3.14159rad)
  Support = -> [YZ_Plane005]
  expr: Constraints[108] = Spreadsheet.mmCellPierceWidth
  expr: Constraints[118] = Spreadsheet.mmCellPierceWidth
  expr: Constraints[128] = Spreadsheet.mmCellPierceWidth
  expr: Constraints[138] = Spreadsheet.mmCellPierceWidth
  expr: Constraints[148] = Spreadsheet.mmCellPierceWidth
  expr: Constraints[158] = Spreadsheet.mmCellPierceWidth
  expr: Constraints[171] = Spreadsheet.mmCellWidth + Spreadsheet.mmCellWall
  expr: Constraints[172] = Spreadsheet.mmCellWidth + Spreadsheet.mmCellWall
  expr: Constraints[173] = Spreadsheet.mmCellWidth + Spreadsheet.mmCellWall
  expr: Constraints[174] = Spreadsheet.mmCellWidth + Spreadsheet.mmCellWall
  expr: Constraints[175] = Spreadsheet.mmCellWidth + Spreadsheet.mmCellWall
  expr: Constraints[176] = Spreadsheet.mmCellWidth + Spreadsheet.mmCellWall
  expr: Constraints[178] = Spreadsheet.mmCellWidth / 2
  expr: Constraints[179] = Spreadsheet.mmCellWidth / 2
  expr: Constraints[180] = Spreadsheet.mmCommonBaseLenght + Spreadsheet.mmToothStep * 1.5
  expr: Constraints[181] = Spreadsheet.mmToothStep * 2
  expr: Constraints[19] = Spreadsheet.mmCellPierceWidth
  expr: Constraints[29] = Spreadsheet.mmCellPierceWidth
  expr: Constraints[39] = Spreadsheet.mmCellPierceWidth
  expr: Constraints[49] = Spreadsheet.mmCellPierceWidth
  expr: Constraints[59] = Spreadsheet.mmCellPierceWidth
  expr: Constraints[69] = Spreadsheet.mmCellPierceWidth
  expr: Constraints[82] = Spreadsheet.mmCellWidth + Spreadsheet.mmCellWall
  expr: Constraints[83] = Spreadsheet.mmCellWidth + Spreadsheet.mmCellWall
  expr: Constraints[84] = Spreadsheet.mmCellWidth + Spreadsheet.mmCellWall
  expr: Constraints[85] = Spreadsheet.mmCellWidth + Spreadsheet.mmCellWall
  expr: Constraints[86] = Spreadsheet.mmCellWidth + Spreadsheet.mmCellWall
  expr: Constraints[87] = Spreadsheet.mmCellWidth + Spreadsheet.mmCellWall
  expr: Constraints[98] = Spreadsheet.mmCellPierceWidth
  expr: Constraints[9] = Spreadsheet.mmCellPierceWidth
  sketch-geometry (56):
    g0: ArcOfCircle CenterX=29 CenterY=0 CenterZ=0 NormalX=0 NormalY=0 NormalZ=1 AngleXU=0 Radius=3.0104 StartAngle=2.41495 EndAngle=3.86823
    g1: LineSegment StartX=26.75 StartY=2 StartZ=0 EndX=31.25 EndY=2 EndZ=0
    g2: LineSegment StartX=26.75 StartY=-2 StartZ=0 EndX=31.25 EndY=-2 EndZ=0
    g3: ArcOfCircle CenterX=29 CenterY=0 CenterZ=0 NormalX=0 NormalY=0 NormalZ=1 AngleXU=0 Radius=3.0104 StartAngle=5.55654 EndAngle=7.00983
    g4: ArcOfCircle CenterX=29 CenterY=9.8 CenterZ=0 NormalX=0 NormalY=0 NormalZ=1 AngleXU=0 Radius=3.0104 StartAngle=2.41495 EndAngle=3.86823
    g5: LineSegment StartX=26.75 StartY=11.8 StartZ=0 EndX=31.25 EndY=11.8 EndZ=0
    g6: LineSegment StartX=26.75 StartY=7.8 StartZ=0 EndX=31.25 EndY=7.8 EndZ=0
    g7: ArcOfCircle CenterX=29 CenterY=9.8 CenterZ=0 NormalX=0 NormalY=0 NormalZ=1 AngleXU=0 Radius=3.0104 StartAngle=5.55654 EndAngle=7.00983
    g8: ArcOfCircle CenterX=29 CenterY=19.6 CenterZ=0 NormalX=0 NormalY=0 NormalZ=1 AngleXU=0 Radius=3.0104 StartAngle=2.41495 EndAngle=3.86823
    g9: LineSegment StartX=26.75 StartY=21.6 StartZ=0 EndX=31.25 EndY=21.6 EndZ=0
    g10: LineSegment StartX=26.75 StartY=17.6 StartZ=0 EndX=31.25 EndY=17.6 EndZ=0
    g11: ArcOfCircle CenterX=29 CenterY=19.6 CenterZ=0 NormalX=0 NormalY=0 NormalZ=1 AngleXU=0 Radius=3.0104 StartAngle=5.55654 EndAngle=7.00983
    g12: ArcOfCircle CenterX=29 CenterY=29.4 CenterZ=0 NormalX=0 NormalY=0 NormalZ=1 AngleXU=0 Radius=3.0104 StartAngle=2.41495 EndAngle=3.86823
    g13: LineSegment StartX=26.75 StartY=31.4 StartZ=0 EndX=31.25 EndY=31.4 EndZ=0
    g14: LineSegment StartX=26.75 StartY=27.4 StartZ=0 EndX=31.25 EndY=27.4 EndZ=0
    g15: ArcOfCircle CenterX=29 CenterY=29.4 CenterZ=0 NormalX=0 NormalY=0 NormalZ=1 AngleXU=0 Radius=3.0104 StartAngle=5.55654 EndAngle=7.00983
    g16: ArcOfCircle CenterX=29 CenterY=-9.8 CenterZ=0 NormalX=0 NormalY=0 NormalZ=1 AngleXU=0 Radius=3.0104 StartAngle=2.41495 EndAngle=3.86823
    g17: LineSegment StartX=26.75 StartY=-7.8 StartZ=0 EndX=31.25 EndY=-7.8 EndZ=0
    g18: LineSegment StartX=26.75 StartY=-11.8 StartZ=0 EndX=31.25 EndY=-11.8 EndZ=0
    g19: ArcOfCircle CenterX=29 CenterY=-9.8 CenterZ=0 NormalX=0 NormalY=0 NormalZ=1 AngleXU=0 Radius=3.0104 StartAngle=5.55654 EndAngle=7.00983
    g20: ArcOfCircle CenterX=29 CenterY=-19.6 CenterZ=0 NormalX=0 NormalY=0 NormalZ=1 AngleXU=0 Radius=3.0104 StartAngle=2.41495 EndAngle=3.86823
    g21: LineSegment StartX=26.75 StartY=-17.6 StartZ=0 EndX=31.25 EndY=-17.6 EndZ=0
    g22: LineSegment StartX=26.75 StartY=-21.6 StartZ=0 EndX=31.25 EndY=-21.6 EndZ=0
    g23: ArcOfCircle CenterX=29 CenterY=-19.6 CenterZ=0 NormalX=0 NormalY=0 NormalZ=1 AngleXU=0 Radius=3.0104 StartAngle=5.55654 EndAngle=7.00983
    g24: ArcOfCircle CenterX=29 CenterY=-29.4 CenterZ=0 NormalX=0 NormalY=0 NormalZ=1 AngleXU=0 Radius=3.0104 StartAngle=2.41495 EndAngle=3.86823
    g25: LineSegment StartX=26.75 StartY=-27.4 StartZ=0 EndX=31.25 EndY=-27.4 EndZ=0
    g26: LineSegment StartX=26.75 StartY=-31.4 StartZ=0 EndX=31.25 EndY=-31.4 EndZ=0
    g27: ArcOfCircle CenterX=29 CenterY=-29.4 CenterZ=0 NormalX=0 NormalY=0 NormalZ=1 AngleXU=0 Radius=3.0104 StartAngle=5.55654 EndAngle=7.00983
    g28: ArcOfCircle CenterX=15 CenterY=0 CenterZ=0 NormalX=0 NormalY=0 NormalZ=1 AngleXU=0 Radius=3.0104 StartAngle=2.41495 EndAngle=3.86823
    g29: LineSegment StartX=12.75 StartY=2 StartZ=0 EndX=17.25 EndY=2 EndZ=0
    g30: LineSegment StartX=12.75 StartY=-2 StartZ=0 EndX=17.25 EndY=-2 EndZ=0
    g31: ArcOfCircle CenterX=15 CenterY=0 CenterZ=0 NormalX=0 NormalY=0 NormalZ=1 AngleXU=0 Radius=3.0104 StartAngle=5.55654 EndAngle=7.00983
    g32: ArcOfCircle CenterX=15 CenterY=9.8 CenterZ=0 NormalX=0 NormalY=0 NormalZ=1 AngleXU=0 Radius=3.0104 StartAngle=2.41495 EndAngle=3.86823
    g33: LineSegment StartX=12.75 StartY=11.8 StartZ=0 EndX=17.25 EndY=11.8 EndZ=0
    g34: LineSegment StartX=12.75 StartY=7.8 StartZ=0 EndX=17.25 EndY=7.8 EndZ=0
    g35: ArcOfCircle CenterX=15 CenterY=9.8 CenterZ=0 NormalX=0 NormalY=0 NormalZ=1 AngleXU=0 Radius=3.0104 StartAngle=5.55654 EndAngle=7.00983
    g36: ArcOfCircle CenterX=15 CenterY=19.6 CenterZ=0 NormalX=0 NormalY=0 NormalZ=1 AngleXU=0 Radius=3.0104 StartAngle=2.41495 EndAngle=3.86823
    g37: LineSegment StartX=12.75 StartY=21.6 StartZ=0 EndX=17.25 EndY=21.6 EndZ=0
    g38: LineSegment StartX=12.75 StartY=17.6 StartZ=0 EndX=17.25 EndY=17.6 EndZ=0
    g39: ArcOfCircle CenterX=15 CenterY=19.6 CenterZ=0 NormalX=0 NormalY=0 NormalZ=1 AngleXU=0 Radius=3.0104 StartAngle=5.55654 EndAngle=7.00983
    g40: ArcOfCircle CenterX=15 CenterY=29.4 CenterZ=0 NormalX=0 NormalY=0 NormalZ=1 AngleXU=0 Radius=3.0104 StartAngle=2.41495 EndAngle=3.86823
    g41: LineSegment StartX=12.75 StartY=31.4 StartZ=0 EndX=17.25 EndY=31.4 EndZ=0
    g42: LineSegment StartX=12.75 StartY=27.4 StartZ=0 EndX=17.25 EndY=27.4 EndZ=0
    g43: ArcOfCircle CenterX=15 CenterY=29.4 CenterZ=0 NormalX=0 NormalY=0 NormalZ=1 AngleXU=0 Radius=3.0104 StartAngle=5.55654 EndAngle=7.00983
    g44: ArcOfCircle CenterX=15 CenterY=-9.8 CenterZ=0 NormalX=0 NormalY=0 NormalZ=1 AngleXU=0 Radius=3.0104 StartAngle=2.41495 EndAngle=3.86823
    g45: LineSegment StartX=12.75 StartY=-7.8 StartZ=0 EndX=17.25 EndY=-7.8 EndZ=0
    g46: LineSegment StartX=12.75 StartY=-11.8 StartZ=0 EndX=17.25 EndY=-11.8 EndZ=0
    g47: ArcOfCircle CenterX=15 CenterY=-9.8 CenterZ=0 NormalX=0 NormalY=0 NormalZ=1 AngleXU=0 Radius=3.0104 StartAngle=5.55654 EndAngle=7.00983
    g48: ArcOfCircle CenterX=15 CenterY=-19.6 CenterZ=0 NormalX=0 NormalY=0 NormalZ=1 AngleXU=0 Radius=3.0104 StartAngle=2.41495 EndAngle=3.86823
    g49: LineSegment StartX=12.75 StartY=-17.6 StartZ=0 EndX=17.25 EndY=-17.6 EndZ=0
    g50: LineSegment StartX=12.75 StartY=-21.6 StartZ=0 EndX=17.25 EndY=-21.6 EndZ=0
    g51: ArcOfCircle CenterX=15 CenterY=-19.6 CenterZ=0 NormalX=0 NormalY=0 NormalZ=1 AngleXU=0 Radius=3.0104 StartAngle=5.55654 EndAngle=7.00983
    g52: ArcOfCircle CenterX=15 CenterY=-29.4 CenterZ=0 NormalX=0 NormalY=0 NormalZ=1 AngleXU=0 Radius=3.0104 StartAngle=2.41495 EndAngle=3.86823
    g53: LineSegment StartX=12.75 StartY=-27.4 StartZ=0 EndX=17.25 EndY=-27.4 EndZ=0
    g54: LineSegment StartX=12.75 StartY=-31.4 StartZ=0 EndX=17.25 EndY=-31.4 EndZ=0
    g55: ArcOfCircle CenterX=15 CenterY=-29.4 CenterZ=0 NormalX=0 NormalY=0 NormalZ=1 AngleXU=0 Radius=3.0104 StartAngle=5.55654 EndAngle=7.00983
  constraints (182):
    c: Horizontal(g1)
    c: Horizontal(g2)
    c: PointOnObject(g1,g0)
    c: Coincident(g0,g3)
    c: Coincident(g0,g2)
    c: Coincident(g3,g2)
    c: Coincident(g1,g0)
    c: Coincident(g3,g1)
    c: Equal(g2,g1)
    c: DistanceY(g2,g1) = 4
    c: Horizontal(g5)
    c: Horizontal(g6)
    c: PointOnObject(g5,g4)
    c: Coincident(g4,g7)
    c: Coincident(g4,g6)
    c: Coincident(g7,g6)
    c: Coincident(g5,g4)
    c: Coincident(g7,g5)
    c: Equal(g6,g5)
    c: DistanceY(g6,g5) = 4
    c: Horizontal(g9)
    c: Horizontal(g10)
    c: PointOnObject(g9,g8)
    c: Coincident(g8,g11)
    c: Coincident(g8,g10)
    c: Coincident(g11,g10)
    c: Coincident(g9,g8)
    c: Coincident(g11,g9)
    c: Equal(g10,g9)
    c: DistanceY(g10,g9) = 4
    c: Horizontal(g13)
    c: Horizontal(g14)
    c: PointOnObject(g13,g12)
    c: Coincident(g12,g15)
    c: Coincident(g12,g14)
    c: Coincident(g15,g14)
    c: Coincident(g13,g12)
    c: Coincident(g15,g13)
    c: Equal(g14,g13)
    c: DistanceY(g14,g13) = 4
    c: Horizontal(g17)
    c: Horizontal(g18)
    c: PointOnObject(g17,g16)
    c: Coincident(g16,g19)
    c: Coincident(g16,g18)
    c: Coincident(g19,g18)
    c: Coincident(g17,g16)
    c: Coincident(g19,g17)
    c: Equal(g18,g17)
    c: DistanceY(g18,g17) = 4
    c: Horizontal(g21)
    c: Horizontal(g22)
    c: PointOnObject(g21,g20)
    c: Coincident(g20,g23)
    c: Coincident(g20,g22)
    c: Coincident(g23,g22)
    c: Coincident(g21,g20)
    c: Coincident(g23,g21)
    c: Equal(g22,g21)
    c: DistanceY(g22,g21) = 4
    c: Horizontal(g25)
    c: Horizontal(g26)
    c: PointOnObject(g25,g24)
    c: Coincident(g24,g27)
    c: Coincident(g24,g26)
    c: Coincident(g27,g26)
    c: Coincident(g25,g24)
    c: Coincident(g27,g25)
    c: Equal(g26,g25)
    c: DistanceY(g26,g25) = 4
    c: Vertical(g0,g4)
    c: Vertical(g4,g8)
    c: Vertical(g8,g12)
    c: Vertical(g12,g16)
    c: Vertical(g16,g20)
    c: Vertical(g20,g24)
    c: Equal(g2,g18)
    c: Equal(g18,g22)
    c: Equal(g22,g26)
    c: Equal(g1,g5)
    c: Equal(g5,g9)
    c: Equal(g9,g13)
    c: DistanceY(g8,g12) = 9.8
    c: DistanceY(g4,g8) = 9.8
    c: DistanceY(g0,g4) = 9.8
    c: DistanceY(g16,g0) = 9.8
    c: DistanceY(g20,g16) = 9.8
    c: DistanceY(g24,g20) = 9.8
    c: PointOnObject(g0,g-1)
    c: Horizontal(g29)
    c: Horizontal(g30)
    c: PointOnObject(g29,g28)
    c: Coincident(g28,g31)
    c: Coincident(g28,g30)
    c: Coincident(g31,g30)
    c: Coincident(g29,g28)
    c: Coincident(g31,g29)
    c: Equal(g30,g29)
    c: DistanceY(g30,g29) = 4
    c: Horizontal(g33)
    c: Horizontal(g34)
    c: PointOnObject(g33,g32)
    c: Coincident(g32,g35)
    c: Coincident(g32,g34)
    c: Coincident(g35,g34)
    c: Coincident(g33,g32)
    c: Coincident(g35,g33)
    c: Equal(g34,g33)
    c: DistanceY(g34,g33) = 4
    c: Horizontal(g37)
    c: Horizontal(g38)
    c: PointOnObject(g37,g36)
    c: Coincident(g36,g39)
    c: Coincident(g36,g38)
    c: Coincident(g39,g38)
    c: Coincident(g37,g36)
    c: Coincident(g39,g37)
    c: Equal(g38,g37)
    c: DistanceY(g38,g37) = 4
    c: Horizontal(g41)
    c: Horizontal(g42)
    c: PointOnObject(g41,g40)
    c: Coincident(g40,g43)
    c: Coincident(g40,g42)
    c: Coincident(g43,g42)
    c: Coincident(g41,g40)
    c: Coincident(g43,g41)
    c: Equal(g42,g41)
    c: DistanceY(g42,g41) = 4
    c: Horizontal(g45)
    c: Horizontal(g46)
    c: PointOnObject(g45,g44)
    c: Coincident(g44,g47)
    c: Coincident(g44,g46)
    c: Coincident(g47,g46)
    c: Coincident(g45,g44)
    c: Coincident(g47,g45)
    c: Equal(g46,g45)
    c: DistanceY(g46,g45) = 4
    c: Horizontal(g49)
    c: Horizontal(g50)
    c: PointOnObject(g49,g48)
    c: Coincident(g48,g51)
    c: Coincident(g48,g50)
    c: Coincident(g51,g50)
    c: Coincident(g49,g48)
    c: Coincident(g51,g49)
    c: Equal(g50,g49)
    c: DistanceY(g50,g49) = 4
    c: Horizontal(g53)
    c: Horizontal(g54)
    c: PointOnObject(g53,g52)
    c: Coincident(g52,g55)
    c: Coincident(g52,g54)
    c: Coincident(g55,g54)
    c: Coincident(g53,g52)
    c: Coincident(g55,g53)
    c: Equal(g54,g53)
    c: DistanceY(g54,g53) = 4
    c: Vertical(g28,g32)
    c: Vertical(g32,g36)
    c: Vertical(g36,g40)
    c: Vertical(g40,g44)
    c: Vertical(g44,g48)
    c: Vertical(g48,g52)
    c: Equal(g30,g46)
    c: Equal(g46,g50)
    c: Equal(g50,g54)
    c: Equal(g29,g33)
    c: Equal(g33,g37)
    c: Equal(g37,g41)
    c: DistanceY(g36,g40) = 9.8
    c: DistanceY(g32,g36) = 9.8
    c: DistanceY(g28,g32) = 9.8
    c: DistanceY(g44,g28) = 9.8
    c: DistanceY(g48,g44) = 9.8
    c: DistanceY(g52,g48) = 9.8
    c: PointOnObject(g28,g-1)
    c: DistanceX(g24,g26) = 4.5
    c: DistanceX(g52,g54) = 4.5
    c: DistanceX(g-1,g28) = 15
    c: DistanceX(g28,g0) = 14
FEATURE [PartDesign::Pocket] Pocket  label="PiercesPocket"
  BaseFeature = -> Pad
  Direction = (-2e-16,2e-16,1)
  Length = 69.4
  Length2 = 5
  Midplane = true
  Profile = -> Sketch
  ReferenceAxis = -> Sketch [N_Axis]
  Type = 0
  expr: Length = Spreadsheet.mmBaseWidth + Spreadsheet.mmCellWall * 2
FEATURE [PartDesign::Body] Body004  label="BeamFixator"
  Group = -> [Sketch022,Pad,Sketch,Pocket]
  Origin = -> Origin005
  Tip = -> Pocket
COMPONENT P1 — recipe-attached ("HingePart", modeled in this document).
Construction recipe (the document's own serialized feature program — sketch geometry with constraints, then the solid features built on it; lengths are millimeters unless a unit is written):

FEATURE [PartDesign::LinearPattern] LinearPattern
  Direction = -> Sketch007 [V_Axis]
  Length = 67.8
  Occurrences = 4
  Originals = -> [Revolution,Revolution004,Pocket001,Pocket002,Pad008,Pad009,Pad010,Pad011,Pocket004,Pocket005]
  expr: Length = Spreadsheet.mmHingeHight
  expr: Occurrences = Spreadsheet.nHingeHightDiskCnt
FEATURE [PartDesign::Body] Body005
  Group = -> [LinearPattern]
  Origin = -> Origin007
  Tip = -> LinearPattern
COMPONENT P2 — recipe-attached ("AxisFixatorPart", modeled in this document).
Construction recipe (the document's own serialized feature program — sketch geometry with constraints, then the solid features built on it; lengths are millimeters unless a unit is written):

FEATURE [Sketcher::SketchObject] Sketch027  label="CommonFixatorScatch"
  FullyConstrained = false
  MapMode = 5
  Placement = pos=(0,0,0) rot=(0.57735,0.57735,0.57735;2.0944rad)
  Support = -> [YZ_Plane013]
  expr: Constraints[0] = Spreadsheet.mmAxisTubeDia + 2 * Spreadsheet.mmFixatorThick + 2 * Spreadsheet.mmTwoSideTapeThick
  expr: Constraints[17] = Spreadsheet.mmAxisTubeDia / 2 + Spreadsheet.mmPetalHightMax + Spreadsheet.mmTwoSideTapeThick
  expr: Constraints[18] = Spreadsheet.mmAxisTubeDia / 2 + Spreadsheet.mmPetalHightMax + Spreadsheet.mmTwoSideTapeThick
  expr: Constraints[32] = Spreadsheet.mmPetalPocketWidth
  expr: Constraints[33] = Spreadsheet.mmBaseWidth
  expr: Constraints[3] = Spreadsheet.mmAxisTubeDia
  sketch-geometry (14):
    g0: Circle CenterX=0 CenterY=0 CenterZ=0 NormalX=0 NormalY=0 NormalZ=1 AngleXU=0 Radius=26.72
    g1: LineSegment StartX=0 StartY=0 StartZ=0 EndX=32.2586 EndY=18.6245 EndZ=0
    g2: ArcOfCircle CenterX=0 CenterY=0 CenterZ=0 NormalX=0 NormalY=0 NormalZ=1 AngleXU=0 Radius=20.4 StartAngle=5.32461 EndAngle=6.86682
    g3: LineSegment StartX=-3.7e-15 StartY=-20.4 StartZ=0 EndX=-3.7e-15 EndY=-39.1443 EndZ=0
    g4: LineSegment StartX=-3.7e-15 StartY=-39.1443 StartZ=0 EndX=6.1902 EndY=-42.7183 EndZ=0
    g5: LineSegment StartX=6.1902 StartY=-42.7183 StartZ=0 EndX=40.0902 EndY=15.9983 EndZ=0
    g6: LineSegment StartX=40.0902 StartY=15.9983 StartZ=0 EndX=33.9 EndY=19.5722 EndZ=0
    g7: LineSegment StartX=33.9 StartY=19.5722 StartZ=0 EndX=17.6669 EndY=10.2 EndZ=0
    g8: LineSegment StartX=14.7156 StartY=-14.1284 StartZ=0 EndX=17.9224 EndY=-19.6828 EndZ=0
    g9: LineSegment StartX=17.9224 StartY=-19.6828 StartZ=0 EndX=8.08455 EndY=-25.3627 EndZ=0
    g10: LineSegment StartX=8.08455 StartY=-25.3627 StartZ=0 EndX=4.87772 EndY=-19.8083 EndZ=0
    g11: ArcOfCircle CenterX=0 CenterY=0 CenterZ=0 NormalX=0 NormalY=0 NormalZ=1 AngleXU=0 Radius=20.4 StartAngle=4.71239 EndAngle=4.95383
    g12: ArcOfCircle CenterX=0 CenterY=0 CenterZ=0 NormalX=0 NormalY=0 NormalZ=1 AngleXU=0 Radius=20.4 StartAngle=5.51814 EndAngle=6.80678
    g13: LineSegment StartX=0 StartY=0 StartZ=0 EndX=18.7992 EndY=-32.5612 EndZ=0
  constraints (39):
    c: Diameter(g0) = 53.44
    c: Angle(g-1,g1) = 0.523599
    c: PointOnObject(g6,g1)
    c: Diameter(g2) = 40.8
    c: Vertical(g3)
    c: Coincident(g3,g4)
    c: Coincident(g4,g5)
    c: Coincident(g5,g6)
    c: Coincident(g6,g7)
    c: Coincident(g8,g9)
    c: Coincident(g9,g10)
    c: Equal(g2,g11)
    c: Coincident(g2,g11)
    c: PointOnObject(g3,g-2)
    c: Parallel(g4,g6)
    c: Perpendicular(g5,g4)
    c: Tangent(g0,g5)
    c: Distance(g8,g11) = 26.62
    c: Distance(g9,g11) = 26.62
    c: Coincident(g11,g12)
    c: PointOnObject(g7,g1)
    c: Coincident(g10,g11)
    c: Coincident(g11,g3)
    c: Coincident(g12,g8)
    c: PointOnObject(g12,g1)
    c: Coincident(g12,g7)
    c: PointOnObject(g7,g1)
    c: Perpendicular(g10,g9)
    c: Perpendicular(g9,g8)
    c: Coincident(g13,g11)
    c: Angle(g13,g-1) = 1.0472
    c: Symmetric(g10,g8,g13)
    c: Distance(g10,g8) = 11.3598
    c: Distance(g4,g5) = 67.8
    c: Equal(g4,g6)
    c: Equal(g3,g7)
    c: Coincident(g-1,g0)
    c: Coincident(g0,g11)
    c: Coincident(g11,g1)
FEATURE [PartDesign::Pad] Pad012  label="AxisFixatorBodyPad"
  Direction = (1,-2e-16,3e-16)
  Length = 20.4
  Length2 = 10
  Placement = pos=(0,0,0) rot=(0.57735,0.57735,0.57735;2.0944rad)
  Profile = -> Sketch027
  ReferenceAxis = -> Sketch027 [N_Axis]
  Type = 0
  expr: Length = Spreadsheet.mmFixatorHight
FEATURE [Sketcher::SketchObject] Sketch031  label="MaxPetalBase001"
  FullyConstrained = true
  MapMode = 5
  Placement = pos=(0,0,0) rot=(0.57735,0.57735,0.57735;2.0944rad)
  Support = -> [YZ_Plane013]
  expr: Constraints[3] = Spreadsheet.mmAxisTubeDia / 2 + Spreadsheet.mmPetalHightMax
  expr: Constraints[6] = Spreadsheet.mmAxisTubeDia
  expr: Constraints[8] = Spreadsheet.mmPetalPocketWidth
  sketch-geometry (4):
    g0: LineSegment StartX=19.5933 StartY=5.67991 StartZ=0 EndX=26.52 EndY=5.67991 EndZ=0
    g1: LineSegment StartX=26.52 StartY=5.67991 StartZ=0 EndX=26.52 EndY=-5.67991 EndZ=0
    g2: LineSegment StartX=26.52 StartY=-5.67991 StartZ=0 EndX=19.5933 EndY=-5.67991 EndZ=0
    g3: ArcOfCircle CenterX=0 CenterY=2.5e-15 CenterZ=0 NormalX=0 NormalY=0 NormalZ=1 AngleXU=0 Radius=20.4 StartAngle=6.00103 EndAngle=6.56534
  constraints (12):
    c: Coincident(g0,g1)
    c: Coincident(g1,g2)
    c: Vertical(g1)
    c: DistanceX(g-1,g1) = 26.52
    c: Coincident(g3,g0)
    c: Coincident(g3,g2)
    c: Diameter(g3) = 40.8
    c: Symmetric(g0,g2,g-1)
    c: DistanceY(g2,g0) = 11.3598
    c: Horizontal(g0)
    c: Horizontal(g2)
    c: Coincident(g-1,g3)
FEATURE [Sketcher::SketchObject] Sketch032  label="MinPetalBase001"
  AttachmentOffset = pos=(0,0,18.36) rot=(0,0,1;0rad)
  FullyConstrained = true
  MapMode = 5
  Placement = pos=(18.36,-4.1e-15,4.1e-15) rot=(0.57735,0.57735,0.57735;2.0944rad)
  Support = -> [YZ_Plane013]
  expr: .AttachmentOffset.Base.z = Spreadsheet.mmFixatorHight * 0.9
  expr: Constraints[3] = Spreadsheet.mmAxisTubeDia / 2 + Spreadsheet.mmPetalHightMin
  expr: Constraints[6] = Spreadsheet.mmAxisTubeDia
  expr: Constraints[8] = Spreadsheet.mmPetalPocketWidth
  sketch-geometry (4):
    g0: LineSegment StartX=19.5933 StartY=5.67991 StartZ=0 EndX=23.46 EndY=5.67991 EndZ=0
    g1: LineSegment StartX=23.46 StartY=5.67991 StartZ=0 EndX=23.46 EndY=-5.67991 EndZ=0
    g2: LineSegment StartX=23.46 StartY=-5.67991 StartZ=0 EndX=19.5933 EndY=-5.67991 EndZ=0
    g3: ArcOfCircle CenterX=0 CenterY=2e-15 CenterZ=0 NormalX=0 NormalY=0 NormalZ=1 AngleXU=0 Radius=20.4 StartAngle=6.00103 EndAngle=6.56534
  constraints (12):
    c: Coincident(g0,g1)
    c: Coincident(g1,g2)
    c: Vertical(g1)
    c: DistanceX(g-1,g1) = 23.46
    c: Coincident(g3,g0)
    c: Coincident(g3,g2)
    c: Diameter(g3) = 40.8
    c: Symmetric(g0,g2,g-1)
    c: DistanceY(g2,g0) = 11.3598
    c: Horizontal(g2)
    c: Horizontal(g0)
    c: Coincident(g-1,g3)
FEATURE [PartDesign::SubtractiveLoft] SubtractiveLoft  label="PetalBodySubtractiveLoft"
  BaseFeature = -> Pad012
  Closed = false
  Placement = pos=(0,0,0) rot=(0.57735,0.57735,0.57735;2.0944rad)
  Profile = -> Sketch031
  Ruled = false
  Sections = -> [Sketch032]
FEATURE [PartDesign::PolarPattern] PolarPattern  label="ExisFixatorBodyPolarPattern"
  Angle = 360
  Axis = -> Sketch027 [N_Axis]
  BaseFeature = -> SubtractiveLoft
  Occurrences = 3
  Originals = -> [Pad012,AdditiveLoft,SubtractiveLoft]
  Placement = pos=(0,0,0) rot=(0.57735,0.57735,0.57735;2.0944rad)
FEATURE [PartDesign::Chamfer] Chamfer001
  Angle = 45
  Base = -> PolarPattern [Edge38,Edge9,Edge5,Edge23,Edge65,Edge59,Edge69,Edge47,Edge41]
  BaseFeature = -> PolarPattern
  ChamferType = 1
  FlipDirection = false
  Placement = pos=(0,0,0) rot=(0.57735,0.57735,0.57735;2.0944rad)
  Size = 2
  Size2 = 1
  SupportTransform = false
  UseAllEdges = false
FEATURE [PartDesign::Body] Body007  label="AxisFixatorBody"
  Group = -> [Sketch027,Pad012,Sketch031,Sketch032,SubtractiveLoft,PolarPattern,Chamfer001]
  Origin = -> Origin013
  Tip = -> Chamfer001
COMPONENT P3 — recipe-attached ("PetalMountingTemplate", modeled in this document).
Construction recipe (the document's own serialized feature program — sketch geometry with constraints, then the solid features built on it; lengths are millimeters unless a unit is written):

FEATURE [Sketcher::SketchObject] Sketch035  label="CommonFixatorScatch001"
  AttachmentOffset = pos=(0,0,16.32) rot=(0,0,1;0rad)
  FullyConstrained = false
  MapMode = 5
  Placement = pos=(16.32,-3.6e-15,3.6e-15) rot=(0.57735,0.57735,0.57735;2.0944rad)
  Support = -> [YZ_Plane013]
  expr: .AttachmentOffset.Base.z = Spreadsheet.mmFixatorHight * 0.8
  expr: Constraints[0] = Spreadsheet.mmAxisTubeDia + 2 * Spreadsheet.mmFixatorThick
  expr: Constraints[24] = Spreadsheet.mmBaseWidth
  expr: Constraints[3] = Spreadsheet.mmAxisTubeDia
  sketch-geometry (9):
    g0: Circle CenterX=0 CenterY=0 CenterZ=0 NormalX=0 NormalY=0 NormalZ=1 AngleXU=0 Radius=26.62
    g1: LineSegment StartX=0 StartY=0 StartZ=0 EndX=49.303 EndY=28.4651 EndZ=0
    g2: ArcOfCircle CenterX=0 CenterY=0 CenterZ=0 NormalX=0 NormalY=0 NormalZ=1 AngleXU=0 Radius=20.4 StartAngle=4.71235 EndAngle=6.7955
    g3: LineSegment StartX=-3.7e-15 StartY=-20.4 StartZ=0 EndX=-3.7e-15 EndY=-39.1443 EndZ=0
    g4: LineSegment StartX=-3.7e-15 StartY=-39.1443 StartZ=0 EndX=6.1036 EndY=-42.6683 EndZ=0
    g5: LineSegment StartX=6.1036 StartY=-42.6683 StartZ=0 EndX=40.0036 EndY=16.0483 EndZ=0
    g6: LineSegment StartX=40.0036 StartY=16.0483 StartZ=0 EndX=33.9 EndY=19.5722 EndZ=0
    g7: LineSegment StartX=33.9 StartY=19.5722 StartZ=0 EndX=17.6669 EndY=10.2 EndZ=0
    g8: ArcOfCircle CenterX=0 CenterY=0 CenterZ=0 NormalX=0 NormalY=0 NormalZ=1 AngleXU=0 Radius=20.4 StartAngle=4.71239 EndAngle=6.80678
  constraints (25):
    c: Diameter(g0) = 53.24
    c: Angle(g-1,g1) = 0.523599
    c: PointOnObject(g6,g1)
    c: Diameter(g2) = 40.8
    c: Vertical(g3)
    c: Coincident(g3,g4)
    c: Coincident(g4,g5)
    c: Coincident(g5,g6)
    c: Coincident(g6,g7)
    c: PointOnObject(g3,g-2)
    c: Parallel(g4,g6)
    c: Perpendicular(g5,g4)
    c: Tangent(g0,g5)
    c: PointOnObject(g8,g1)
    c: Coincident(g8,g7)
    c: PointOnObject(g8,g-2)
    c: PointOnObject(g8,g-1)
    c: PointOnObject(g8,g2)
    c: Coincident(g3,g8)
    c: Equal(g4,g6)
    c: Equal(g7,g3)
    c: Coincident(g2,g1)
    c: Coincident(g8,g1)
    c: Coincident(g8,g0)
    c: Distance(g4,g5) = 67.8
FEATURE [PartDesign::Pad] Pad013  label="AxisFixatorBodyPad001"
  Direction = (1,-2e-16,3e-16)
  Length = 6.12
  Length2 = 10
  Placement = pos=(0,0,0) rot=(0.57735,0.57735,0.57735;2.0944rad)
  Profile = -> Sketch035
  ReferenceAxis = -> Sketch035 [N_Axis]
  Type = 0
  expr: Length = Spreadsheet.mmFixatorHight * 0.3
FEATURE [Sketcher::SketchObject] Sketch038  label="MaxPetalBase004"
  FullyConstrained = true
  MapMode = 5
  Placement = pos=(0,0,0) rot=(0.57735,0.57735,0.57735;2.0944rad)
  Support = -> [YZ_Plane013]
  expr: Constraints[11] = Spreadsheet.mmPetalPocketWidth
  expr: Constraints[3] = Spreadsheet.mmAxisTubeDia * 2
  expr: Constraints[6] = Spreadsheet.mmAxisTubeDia
  sketch-geometry (4):
    g0: LineSegment StartX=19.5933 StartY=5.67991 StartZ=0 EndX=81.6 EndY=5.67991 EndZ=0
    g1: LineSegment StartX=81.6 StartY=5.67991 StartZ=0 EndX=81.6 EndY=-5.67991 EndZ=0
    g2: LineSegment StartX=81.6 StartY=-5.67991 StartZ=0 EndX=19.5933 EndY=-5.67991 EndZ=0
    g3: ArcOfCircle CenterX=0 CenterY=2.5e-15 CenterZ=0 NormalX=0 NormalY=0 NormalZ=1 AngleXU=0 Radius=20.4 StartAngle=6.00103 EndAngle=6.56534
  constraints (12):
    c: Coincident(g0,g1)
    c: Coincident(g1,g2)
    c: Vertical(g1)
    c: DistanceX(g-1,g1) = 81.6
    c: Coincident(g3,g0)
    c: Coincident(g3,g2)
    c: Diameter(g3) = 40.8
    c: Horizontal(g0)
    c: Horizontal(g2)
    c: PointOnObject(g3,g-2)
    c: Symmetric(g0,g2,g-1)
    c: DistanceY(g2,g0) = 11.3598
FEATURE [Sketcher::SketchObject] Sketch039  label="MinPetalBase003"
  AttachmentOffset = pos=(0,0,20.4) rot=(0,0,1;0rad)
  FullyConstrained = true
  MapMode = 5
  Placement = pos=(20.4,-4.5e-15,4.5e-15) rot=(0.57735,0.57735,0.57735;2.0944rad)
  Support = -> [YZ_Plane013]
  expr: .AttachmentOffset.Base.z = Spreadsheet.mmFixatorHight
  expr: Constraints[3] = Spreadsheet.mmAxisTubeDia * 2
  expr: Constraints[6] = Spreadsheet.mmAxisTubeDia
  expr: Constraints[7] = Spreadsheet.mmPetalPocketWidth
  sketch-geometry (4):
    g0: LineSegment StartX=19.5933 StartY=5.67991 StartZ=0 EndX=81.6 EndY=5.67991 EndZ=0
    g1: LineSegment StartX=81.6 StartY=5.67991 StartZ=0 EndX=81.6 EndY=-5.67991 EndZ=0
    g2: LineSegment StartX=81.6 StartY=-5.67991 StartZ=0 EndX=19.5933 EndY=-5.67991 EndZ=0
    g3: ArcOfCircle CenterX=0 CenterY=2.1e-15 CenterZ=0 NormalX=0 NormalY=0 NormalZ=1 AngleXU=0 Radius=20.4 StartAngle=6.00103 EndAngle=6.56534
  constraints (12):
    c: Coincident(g0,g1)
    c: Coincident(g1,g2)
    c: Vertical(g1)
    c: DistanceX(g-1,g1) = 81.6
    c: Coincident(g3,g0)
    c: Coincident(g3,g2)
    c: Diameter(g3) = 40.8
    c: DistanceY(g2,g0) = 11.3598
    c: Symmetric(g0,g2,g-1)
    c: Coincident(g-1,g3)
    c: Horizontal(g0)
    c: Horizontal(g2)
FEATURE [PartDesign::SubtractiveLoft] SubtractiveLoft001  label="PetalBodySubtractiveLoft001"
  BaseFeature = -> Pad013
  Closed = false
  Placement = pos=(0,0,0) rot=(0.57735,0.57735,0.57735;2.0944rad)
  Profile = -> Sketch038
  Ruled = false
  Sections = -> [Sketch039]
FEATURE [PartDesign::PolarPattern] PolarPattern001  label="ExisFixatorBodyPolarPattern001"
  Angle = 360
  Axis = -> Sketch035 [N_Axis]
  BaseFeature = -> SubtractiveLoft001
  Occurrences = 3
  Originals = -> [Pad013,SubtractiveLoft001]
  Placement = pos=(0,0,0) rot=(0.57735,0.57735,0.57735;2.0944rad)
FEATURE [Sketcher::SketchObject] Sketch040  label="CommonFixatorScatch002"
  AttachmentOffset = pos=(0,0,16.32) rot=(0,0,1;0rad)
  FullyConstrained = true
  MapMode = 5
  Placement = pos=(16.32,-3.6e-15,3.6e-15) rot=(0.57735,0.57735,0.57735;2.0944rad)
  Support = -> [YZ_Plane013]
  expr: .AttachmentOffset.Base.z = Spreadsheet.mmFixatorHight * 0.8
  expr: Constraints[11] = Spreadsheet.mmAxisTubeDia * 2
  expr: Constraints[14] = Spreadsheet.mmTemplatePartsConnectorDia - 2 * Spreadsheet.mmAirSpace
  expr: Constraints[15] = Spreadsheet.mmTemplatePartsConnectorDia * 3 / 2
  expr: Constraints[1] = Spreadsheet.mmAxisTubeDia + 2 * Spreadsheet.mmFixatorThick
  expr: Constraints[27] = Spreadsheet.mmAirSpace
  expr: Constraints[33] = Spreadsheet.mmTemplatePartsConnectorDia / 3
  expr: Constraints[41] = Spreadsheet.mmTemplatePartsConnectorDia
  expr: Constraints[43] = Spreadsheet.mmTemplatePartsConnectorDia * 2 / 3
  expr: Constraints[45] = Spreadsheet.mmTemplatePartsConnectorDia * 2 / 3 - 2 * Spreadsheet.mmAirSpace
  expr: Constraints[52] = Spreadsheet.mmTemplatePartsConnectorDia / 3
  expr: Constraints[55] = Spreadsheet.mmTemplatePartsConnectorDia / 2
  sketch-geometry (19):
    g0: Circle CenterX=0 CenterY=0 CenterZ=0 NormalX=0 NormalY=0 NormalZ=1 AngleXU=0 Radius=40.8
    g1: Circle CenterX=0 CenterY=0 CenterZ=0 NormalX=0 NormalY=0 NormalZ=1 AngleXU=0 Radius=26.62
    g2: LineSegment StartX=-35.5321 StartY=20.0526 StartZ=0 EndX=-28.3499 EndY=15.9059 EndZ=0
    g3: LineSegment StartX=22.767 StartY=-13.6064 StartZ=0 EndX=23.167 EndY=-12.9136 EndZ=0
    g4: LineSegment StartX=23.167 StartY=-12.9136 StartZ=0 EndX=21.4554 EndY=-11.9254 EndZ=0
    g5: LineSegment StartX=-35.1321 StartY=20.7454 StartZ=0 EndX=-35.5321 EndY=20.0526 EndZ=0
    g6: LineSegment StartX=23.0536 StartY=-13.31 StartZ=0 EndX=-35.3338 EndY=20.4 EndZ=0
    g7: ArcOfCircle CenterX=-26.42 CenterY=17.1754 CenterZ=0 NormalX=0 NormalY=0 NormalZ=1 AngleXU=0 Radius=2.31 StartAngle=4.65418 EndAngle=10.0066
    g8: LineSegment StartX=-26.5543 StartY=14.8693 StartZ=0 EndX=18.3629 EndY=-11.0637 EndZ=0
    g9: LineSegment StartX=-29.5129 StartY=17.5011 StartZ=0 EndX=-35.1321 EndY=20.7454 EndZ=0
    g10: LineSegment StartX=-35.1321 StartY=20.7454 StartZ=0 EndX=-35.5321 EndY=20.0526 EndZ=0
    g11: LineSegment StartX=-35.5321 StartY=20.0526 StartZ=0 EndX=22.851 EndY=-13.6549 EndZ=0
    g12: LineSegment StartX=22.851 StartY=-13.6549 StartZ=0 EndX=23.251 EndY=-12.9621 EndZ=0
    g13: LineSegment StartX=23.251 StartY=-12.9621 StartZ=0 EndX=-35.1321 EndY=20.7454 EndZ=0
    g14: ArcOfCircle CenterX=-26.42 CenterY=17.1754 CenterZ=0 NormalX=0 NormalY=0 NormalZ=1 AngleXU=0 Radius=3.11 StartAngle=5.34093 EndAngle=9.31984
    g15: ArcOfCircle CenterX=20.188 CenterY=-12.0474 CenterZ=0 NormalX=0 NormalY=0 NormalZ=1 AngleXU=0 Radius=2.07333 StartAngle=2.64723 EndAngle=5.73035
    g16: ArcOfCircle CenterX=20.188 CenterY=-12.0474 CenterZ=0 NormalX=0 NormalY=0 NormalZ=1 AngleXU=0 Radius=1.27333 StartAngle=1.99844 EndAngle=6.37914
    g17: LineSegment StartX=21.9524 StartY=-13.1361 StartZ=0 EndX=22.767 EndY=-13.6064 EndZ=0
    g18: LineSegment StartX=19.6599 StartY=-10.8888 StartZ=0 EndX=-24.5914 EndY=14.6597 EndZ=0
  constraints (56):
    c: PointOnObject(g6,g0)
    c: Diameter(g1) = 53.24
    c: Coincident(g0,g1)
    c: Coincident(g0,g-1)
    c: Coincident(g3,g4)
    c: Coincident(g9,g5)
    c: Coincident(g5,g2)
    c: Perpendicular(g3,g2)
    c: Symmetric(g2,g9,g6)
    c: Symmetric(g17,g3,g6)
    c: PointOnObject(g0,g6)
    c: Diameter(g0) = 81.6
    c: PointOnObject(g6,g1)
    c: Angle(g-1,g6) = 2.61799
    c: Diameter(g7) = 4.62
    c: Distance(g7,g5) = 9.33
    c: Parallel(g9,g4)
    c: Parallel(g2,g8)
    c: Coincident(g10,g11)
    c: Coincident(g11,g12)
    c: Coincident(g12,g13)
    c: Coincident(g13,g10)
    c: PointOnObject(g10,g0)
    c: Symmetric(g10,g10,g6)
    c: Parallel(g6,g13)
    c: Parallel(g11,g13)
    c: Coincident(g5,g10)
    c: Distance(g3,g3) = 0.8
    c: Coincident(g3,g17)
    c: PointOnObject(g11,g1)
    c: PointOnObject(g12,g1)
    c: PointOnObject(g3,g13)
    c: Distance(g6,g3) = 0.1
    c: Distance(g2,g8) = 2.07333
    c: PointOnObject(g14,g13)
    c: PointOnObject(g14,g13)
    c: PointOnObject(g18,g14)
    c: PointOnObject(g9,g14)
    c: Coincident(g7,g8)
    c: Coincident(g7,g2)
    c: Coincident(g14,g7)
    c: Diameter(g14) = 6.22
    c: PointOnObject(g18,g13)
    c: Diameter(g15) = 4.14667
    c: Coincident(g15,g16)
    c: Diameter(g16) = 2.54667
    c: Coincident(g15,g8)
    c: PointOnObject(g8,g11)
    c: Coincident(g17,g15)
    c: PointOnObject(g15,g11)
    c: Coincident(g4,g16)
    c: Coincident(g18,g16)
    c: Distance(g16,g4) = 2.07333
    c: PointOnObject(g4,g13)
    c: PointOnObject(g16,g13)
    c: Distance(g15,g12) = 3.11
FEATURE [PartDesign::Pocket] Pocket003
  BaseFeature = -> PolarPattern001
  Direction = (-1,2e-16,-3e-16)
  Length = 40.8
  Length2 = 5
  Midplane = true
  Placement = pos=(0,0,0) rot=(0.57735,0.57735,0.57735;2.0944rad)
  Profile = -> Sketch040
  ReferenceAxis = -> Sketch040 [N_Axis]
  Type = 0
  expr: Length = Spreadsheet.mmAxisTubeDia
FEATURE [PartDesign::Chamfer] Chamfer002
  Angle = 45
  Base = -> Pocket003 [Edge1,Edge35,Edge31,Edge98,Edge94,Edge47,Edge12]
  BaseFeature = -> Pocket003
  ChamferType = 0
  FlipDirection = false
  Placement = pos=(0,0,0) rot=(0.57735,0.57735,0.57735;2.0944rad)
  Size = 1
  Size2 = 1
  SupportTransform = false
  UseAllEdges = false
FEATURE [PartDesign::Chamfer] Chamfer003
  Angle = 45
  Base = -> Chamfer002 [Edge56,Edge17,Edge3,Edge28]
  BaseFeature = -> Chamfer002
  ChamferType = 0
  FlipDirection = false
  Placement = pos=(0,0,0) rot=(0.57735,0.57735,0.57735;2.0944rad)
  Size = 1
  Size2 = 1
  SupportTransform = false
  UseAllEdges = false
FEATURE [PartDesign::Chamfer] Chamfer004
  Angle = 45
  Base = -> Chamfer003 [Edge56,Edge61,Edge130,Edge128,Edge73,Edge75]
  BaseFeature = -> Chamfer003
  ChamferType = 0
  FlipDirection = false
  Placement = pos=(0,0,0) rot=(0.57735,0.57735,0.57735;2.0944rad)
  Size = 1
  Size2 = 1
  SupportTransform = false
  UseAllEdges = false
FEATURE [PartDesign::Fillet] Fillet
  Base = -> Chamfer004 [Edge66,Edge26]
  BaseFeature = -> Chamfer004
  Placement = pos=(0,0,0) rot=(0.57735,0.57735,0.57735;2.0944rad)
  Radius = 1
  SupportTransform = false
  UseAllEdges = false
FEATURE [PartDesign::Body] Body010  label="AxisFixatorTemplate"
  Group = -> [Sketch035,Pad013,Sketch038,Sketch039,SubtractiveLoft001,PolarPattern001,Sketch040,Pocket003,Chamfer002,Chamfer003,Chamfer004,Fillet]
  Origin = -> Origin019
  Tip = -> Fillet
COMPONENT P4 — recipe-attached ("AxisFixatorAbsolete", modeled in this document).
Construction recipe (the document's own serialized feature program — sketch geometry with constraints, then the solid features built on it; lengths are millimeters unless a unit is written):

FEATURE [Sketcher::SketchObject] Sketch041  label="CommonFixatorScatch003"
  FullyConstrained = false
  MapMode = 5
  Placement = pos=(0,0,0) rot=(0.57735,0.57735,0.57735;2.0944rad)
  Support = -> [YZ_Plane013]
  expr: Constraints[22] = 2 * (Spreadsheet.mmAxisTubeDia / 2 + Spreadsheet.mmFixatorThick) / cos(Spreadsheet.angPetal / 2)
  expr: Constraints[23] = Spreadsheet.mmHingeHight
  expr: Constraints[31] = Spreadsheet.mmAxisTubeDia
  expr: Constraints[64] = Spreadsheet.mmPetalWidth + Spreadsheet.mmAirSpace
  expr: Constraints[67] = Spreadsheet.mmAxisTubeDia / 2 + Spreadsheet.mmPetalHightMax + Spreadsheet.mmTwoSideTapeThick + Spreadsheet.mmAirSpace
  sketch-geometry (24):
    g0: LineSegment StartX=33.9 StartY=19.5722 StartZ=0 EndX=-33.9 EndY=19.5722 EndZ=0
    g1: LineSegment StartX=-33.9 StartY=19.5722 StartZ=0 EndX=-7.1e-15 EndY=-39.1443 EndZ=0
    g2: LineSegment StartX=-3.7e-15 StartY=-39.1443 StartZ=0 EndX=33.9 EndY=19.5722 EndZ=0
    g3: Circle CenterX=0 CenterY=0 CenterZ=0 NormalX=0 NormalY=0 NormalZ=1 AngleXU=0 Radius=39.1443
    g4: LineSegment StartX=-23.8668 StartY=13.7795 StartZ=0 EndX=-23.8668 EndY=-13.7795 EndZ=0
    g5: LineSegment StartX=-23.8668 StartY=-13.7795 StartZ=0 EndX=0 EndY=-27.5591 EndZ=0
    g6: LineSegment StartX=0 StartY=-27.5591 StartZ=0 EndX=23.8668 EndY=-13.7795 EndZ=0
    g7: LineSegment StartX=23.8668 StartY=-13.7795 StartZ=0 EndX=23.8668 EndY=13.7795 EndZ=0
    g8: LineSegment StartX=23.8668 StartY=13.7795 StartZ=0 EndX=0 EndY=27.5591 EndZ=0
    g9: LineSegment StartX=0 StartY=27.5591 StartZ=0 EndX=-23.8668 EndY=13.7795 EndZ=0
    g10: Circle CenterX=0 CenterY=0 CenterZ=0 NormalX=0 NormalY=0 NormalZ=1 AngleXU=0 Radius=27.5591
    g11: LineSegment StartX=0 StartY=0 StartZ=0 EndX=33.9 EndY=19.5722 EndZ=0
    g12: ArcOfCircle CenterX=0 CenterY=0 CenterZ=0 NormalX=0 NormalY=0 NormalZ=1 AngleXU=0 Radius=20.4 StartAngle=4.5996 EndAngle=6.79538
    g13: LineSegment StartX=-3.7e-15 StartY=-20.4 StartZ=0 EndX=-3.7e-15 EndY=-39.1443 EndZ=0
    g14: LineSegment StartX=-3.7e-15 StartY=-39.1443 StartZ=0 EndX=6.91684 EndY=-43.1378 EndZ=0
    g15: LineSegment StartX=6.91684 StartY=-43.1378 StartZ=0 EndX=40.8168 EndY=15.5787 EndZ=0
    g16: LineSegment StartX=40.8168 StartY=15.5787 StartZ=0 EndX=33.9 EndY=19.5722 EndZ=0
    g17: LineSegment StartX=33.9 StartY=19.5722 StartZ=0 EndX=17.6669 EndY=10.2 EndZ=0
    g18: LineSegment StartX=14.7156 StartY=-14.1284 StartZ=0 EndX=18.6289 EndY=-20.9065 EndZ=0
    g19: LineSegment StartX=18.6289 StartY=-20.9065 StartZ=0 EndX=8.79105 EndY=-26.5864 EndZ=0
    g20: LineSegment StartX=8.79105 StartY=-26.5864 StartZ=0 EndX=4.87772 EndY=-19.8083 EndZ=0
    g21: ArcOfCircle CenterX=0 CenterY=0 CenterZ=0 NormalX=0 NormalY=0 NormalZ=1 AngleXU=0 Radius=20.4 StartAngle=4.71239 EndAngle=4.95383
    g22: ArcOfCircle CenterX=0 CenterY=0 CenterZ=0 NormalX=0 NormalY=0 NormalZ=1 AngleXU=0 Radius=20.4 StartAngle=5.51814 EndAngle=6.80678
    g23: LineSegment StartX=0 StartY=0 StartZ=0 EndX=19.5722 EndY=-33.9 EndZ=0
  constraints (64):
    c: Coincident(g0,g1)
    c: Coincident(g1,g2)
    c: Coincident(g2,g0)
    c: Equal(g0,g1)
    c: Equal(g0,g2)
    c: PointOnObject(g0,g3)
    c: Coincident(g4,g5)
    c: Coincident(g5,g6)
    c: Coincident(g6,g7)
    c: Coincident(g7,g8)
    c: Coincident(g8,g9)
    c: Coincident(g9,g4)
    c: Equal(g4, g5-g9) x5
    c: PointOnObject(g4,g10)
    c: PointOnObject(g5,g10)
    c: PointOnObject(g6,g10)
    c: PointOnObject(g7,g10)
    c: PointOnObject(g8,g10)
    c: Diameter(g10) = 55.1181
    c: Distance(g2) = 67.8
    c: PointOnObject(g5,g-2)
    c: PointOnObject(g4,g10)
    c: Angle(g-1,g11) = 0.523599
    c: Coincident(g3,g10)
    c: Coincident(g3,g11)
    c: Coincident(g3,g-1)
    c: PointOnObject(g0,g11)
    c: Diameter(g12) = 40.8
    c: Coincident(g12,g3)
    c: Vertical(g13)
    c: Coincident(g13,g14)
    c: Coincident(g14,g15)
    c: Coincident(g15,g16)
    c: Coincident(g16,g17)
    c: Coincident(g19,g20)
    c: Coincident(g1,g13)
    c: Coincident(g0,g16)
    c: Equal(g12,g21)
    c: Coincident(g12,g21)
    c: PointOnObject(g13,g-2)
    c: PointOnObject(g13,g3)
    c: Parallel(g2,g15)
    c: Parallel(g14,g16)
    c: Perpendicular(g15,g14)
    c: Tangent(g10,g15)
    c: PointOnObject(g11,g3)
    c: Coincident(g21,g22)
    c: PointOnObject(g17,g11)
    c: Coincident(g20,g21)
    c: Coincident(g21,g13)
    c: Coincident(g22,g18)
    c: PointOnObject(g22,g11)
    c: Coincident(g22,g17)
    c: PointOnObject(g17,g11)
    c: Perpendicular(g20,g19)
    c: Perpendicular(g19,g18)
    c: Coincident(g23,g21)
    c: Angle(g23,g-2) = 2.61799
    c: PointOnObject(g23,g3)
    c: Symmetric(g20,g18,g23)
    c: Distance(g20,g18) = 11.3598
    c: Perpendicular(g23,g19)
    c: Coincident(g18,g19)
    c: Distance(g21,g19) = 27.42
FEATURE [PartDesign::Pad] Pad014  label="AxisFixatorBodyPad002"
  Direction = (1,-2e-16,3e-16)
  Length = 20.4
  Length2 = 10
  Placement = pos=(0,0,0) rot=(0.57735,0.57735,0.57735;2.0944rad)
  Profile = -> Sketch041
  ReferenceAxis = -> Sketch041 [N_Axis]
  Type = 0
  expr: Length = Spreadsheet.mmFixatorHight
FEATURE [Sketcher::SketchObject] Sketch044  label="MaxPetalBase006"
  FullyConstrained = false
  MapMode = 5
  Placement = pos=(0,0,0) rot=(0.57735,0.57735,0.57735;2.0944rad)
  Support = -> [YZ_Plane013]
  expr: Constraints[0] = Spreadsheet.mmAxisTubeDia + 2 * Spreadsheet.mmFixatorThick
  expr: Constraints[14] = Spreadsheet.mmPetalWidth + Spreadsheet.mmAirSpace
  expr: Constraints[1] = Spreadsheet.mmAxisTubeDia
  expr: Constraints[5] = Spreadsheet.mmAxisTubeDia / 2 + Spreadsheet.mmPetalHightMax
  expr: Constraints[9] = Spreadsheet.mmAxisTubeDia
  sketch-geometry (7):
    g0: Circle CenterX=0 CenterY=0 CenterZ=0 NormalX=0 NormalY=0 NormalZ=1 AngleXU=0 Radius=39.855
    g1: Circle CenterX=0 CenterY=0 CenterZ=0 NormalX=0 NormalY=0 NormalZ=1 AngleXU=0 Radius=26.62
    g2: ArcOfCircle CenterX=0 CenterY=0 CenterZ=0 NormalX=0 NormalY=0 NormalZ=1 AngleXU=0 Radius=20.4 StartAngle=5.86249 EndAngle=6.74499
    g3: LineSegment StartX=19.5933 StartY=5.67991 StartZ=0 EndX=26.52 EndY=5.67991 EndZ=0
    g4: LineSegment StartX=26.52 StartY=5.67991 StartZ=0 EndX=26.52 EndY=-5.67991 EndZ=0
    g5: LineSegment StartX=26.52 StartY=-5.67991 StartZ=0 EndX=19.5933 EndY=-5.67991 EndZ=0
    g6: ArcOfCircle CenterX=0 CenterY=0 CenterZ=0 NormalX=0 NormalY=0 NormalZ=1 AngleXU=0 Radius=20.4 StartAngle=6.00103 EndAngle=6.56534
  constraints (22):
    c: Diameter(g1) = 53.24
    c: Diameter(g2) = 40.8
    c: Coincident(g3,g4)
    c: Coincident(g4,g5)
    c: Coincident(g0,g2)
    c: DistanceX(g-1,g4) = 26.52
    c: Coincident(g6,g0)
    c: Coincident(g6,g3)
    c: Coincident(g6,g5)
    c: Diameter(g6) = 40.8
    c: Coincident(g6,g-1)
    c: Symmetric(g3,g5,g-1)
    c: Horizontal(g5)
    c: Horizontal(g3)
    c: DistanceY(g5,g3) = 11.3598
    c: Coincident(g6,g1)
    c: PointOnObject(g6,g-2)
    c: PointOnObject(g6,g-1)
    c: PointOnObject(g6,g5)
    c: PointOnObject(g6,g3)
    c: PointOnObject(g3,g6)
    c: Vertical(g4)
FEATURE [Sketcher::SketchObject] Sketch045  label="MinPetalBase005"
  AttachmentOffset = pos=(0,0,18.36) rot=(0,0,1;0rad)
  FullyConstrained = false
  MapMode = 5
  Placement = pos=(18.36,-4.1e-15,4.1e-15) rot=(0.57735,0.57735,0.57735;2.0944rad)
  Support = -> [YZ_Plane013]
  expr: .AttachmentOffset.Base.z = Spreadsheet.mmFixatorHight * 0.9
  expr: Constraints[0] = Spreadsheet.mmAxisTubeDia + 2 * Spreadsheet.mmFixatorThick
  expr: Constraints[10] = Spreadsheet.mmAxisTubeDia
  expr: Constraints[12] = Spreadsheet.mmPetalWidth + Spreadsheet.mmAirSpace
  expr: Constraints[1] = Spreadsheet.mmAxisTubeDia
  expr: Constraints[6] = Spreadsheet.mmAxisTubeDia / 2 + Spreadsheet.mmPetalHightMin
  sketch-geometry (7):
    g0: Circle CenterX=0 CenterY=2.3e-15 CenterZ=0 NormalX=0 NormalY=0 NormalZ=1 AngleXU=0 Radius=39.844
    g1: Circle CenterX=0 CenterY=2.3e-15 CenterZ=0 NormalX=0 NormalY=0 NormalZ=1 AngleXU=0 Radius=26.62
    g2: ArcOfCircle CenterX=0 CenterY=2.3e-15 CenterZ=0 NormalX=0 NormalY=0 NormalZ=1 AngleXU=0 Radius=20.4 StartAngle=3.8687 EndAngle=6.82101
    g3: LineSegment StartX=19.5933 StartY=5.67991 StartZ=0 EndX=23.46 EndY=5.67991 EndZ=0
    g4: LineSegment StartX=23.46 StartY=5.67991 StartZ=0 EndX=23.46 EndY=-5.67991 EndZ=0
    g5: LineSegment StartX=23.46 StartY=-5.67991 StartZ=0 EndX=19.5933 EndY=-5.67991 EndZ=0
    g6: ArcOfCircle CenterX=0 CenterY=2.3e-15 CenterZ=0 NormalX=0 NormalY=0 NormalZ=1 AngleXU=0 Radius=20.4 StartAngle=6.00103 EndAngle=6.56534
  constraints (17):
    c: Diameter(g1) = 53.24
    c: Diameter(g2) = 40.8
    c: Coincident(g3,g4)
    c: Coincident(g4,g5)
    c: Coincident(g0,g2)
    c: Vertical(g4)
    c: DistanceX(g-1,g4) = 23.46
    c: Coincident(g6,g0)
    c: Coincident(g6,g3)
    c: Coincident(g6,g5)
    c: Diameter(g6) = 40.8
    c: Symmetric(g3,g5,g-1)
    c: DistanceY(g5,g3) = 11.3598
    c: Horizontal(g3)
    c: Horizontal(g5)
    c: Coincident(g6,g1)
    c: Coincident(g6,g-1)
FEATURE [PartDesign::SubtractiveLoft] SubtractiveLoft002  label="PetalBodySubtractiveLoft002"
  BaseFeature = -> Pad014
  Closed = false
  Placement = pos=(0,0,0) rot=(0.57735,0.57735,0.57735;2.0944rad)
  Profile = -> Sketch044
  Ruled = false
  Sections = -> [Sketch045]
FEATURE [PartDesign::PolarPattern] PolarPattern002  label="ExisFixatorBodyPolarPattern002"
  Angle = 360
  Axis = -> Sketch041 [N_Axis]
  BaseFeature = -> SubtractiveLoft002
  Occurrences = 3
  Originals = -> [Pad014,SubtractiveLoft002]
  Placement = pos=(0,0,0) rot=(0.57735,0.57735,0.57735;2.0944rad)
FEATURE [PartDesign::Body] Body011  label="AxisFixatorBody001"
  Group = -> [Sketch041,Pad014,Sketch044,Sketch045,SubtractiveLoft002,PolarPattern002]
  Origin = -> Origin021
  Tip = -> PolarPattern002
COMPONENT P5 — recipe-attached ("PulleyOnRotor", modeled in this document).
Construction recipe (the document's own serialized feature program — sketch geometry with constraints, then the solid features built on it; lengths are millimeters unless a unit is written):

FEATURE [Sketcher::SketchObject] Sketch048
  FullyConstrained = true
  MapMode = 5
  Support = -> [XY_Plane019]
  expr: Constraints[1] = Spreadsheet.mmPulleyIntDia
  expr: Constraints[24] = Spreadsheet.mmPulleyExtDia + Spreadsheet.mmPasBaseType + Spreadsheet.mmPassToothHight * 2
  expr: Constraints[38] = 360 / Spreadsheet.cntPulleyTooth
  expr: Constraints[4] = Spreadsheet.mmPulleyExtDia
  expr: Constraints[5] = Spreadsheet.mmPulleyExtDia + Spreadsheet.mmPassToothHight * 2
  sketch-geometry (13):
    g0: ArcOfCircle CenterX=0 CenterY=0 CenterZ=0 NormalX=0 NormalY=0 NormalZ=1 AngleXU=0 Radius=26.4 StartAngle=0 EndAngle=0.15708
    g1: Circle CenterX=0 CenterY=0 CenterZ=0 NormalX=0 NormalY=0 NormalZ=1 AngleXU=0 Radius=29.181
    g2: Circle CenterX=0 CenterY=0 CenterZ=0 NormalX=0 NormalY=0 NormalZ=1 AngleXU=0 Radius=31.081
    g3: LineSegment StartX=0 StartY=0 StartZ=0 EndX=31.4391 EndY=4.97946 EndZ=0
    g4: LineSegment StartX=0 StartY=0 StartZ=0 EndX=31.831 EndY=0 EndZ=0
    g5: LineSegment StartX=30.6983 StartY=4.86214 StartZ=0 EndX=26.075 EndY=4.12987 EndZ=0
    g6: LineSegment StartX=31.081 StartY=0 StartZ=0 EndX=26.4 EndY=0 EndZ=0
    g7: ArcOfCircle CenterX=29.5131 CenterY=4.67442 CenterZ=0 NormalX=0 NormalY=0 NormalZ=1 AngleXU=0 Radius=1.2 StartAngle=4.80863 EndAngle=6.44026
    g8: ArcOfCircle CenterX=29.881 CenterY=0 CenterZ=0 NormalX=0 NormalY=0 NormalZ=1 AngleXU=0 Radius=1.2 StartAngle=0 EndAngle=1.63164
    g9: ArcOfCircle CenterX=29.6904 CenterY=2.83823 CenterZ=0 NormalX=0 NormalY=0 NormalZ=1 AngleXU=0 Radius=0.644724 StartAngle=1.66703 EndAngle=3.88293
    g10: ArcOfCircle CenterX=29.7688 CenterY=1.84131 CenterZ=0 NormalX=0 NormalY=0 NormalZ=1 AngleXU=0 Radius=0.644724 StartAngle=2.55733 EndAngle=4.77323
    g11: ArcOfCircle CenterX=29.091 CenterY=2.28951 CenterZ=0 NormalX=0 NormalY=0 NormalZ=1 AngleXU=0 Radius=0.167853 StartAngle=5.69893 EndAngle=7.02452
    g12: Circle CenterX=0 CenterY=0 CenterZ=0 NormalX=0 NormalY=0 NormalZ=1 AngleXU=0 Radius=31.831
  constraints (39):
    c: Coincident(g0,g-1)
    c: Diameter(g0) = 52.8
    c: Coincident(g1,g0)
    c: Coincident(g2,g0)
    c: Diameter(g1) = 58.362
    c: Diameter(g2) = 62.162
    c: Coincident(g4,g3)
    c: Coincident(g0,g3)
    c: PointOnObject(g6,g0)
    c: PointOnObject(g0,g4)
    c: PointOnObject(g6,g4)
    c: Distance(g7,g5) = 1.2
    c: PointOnObject(g8,g4)
    c: Distance(g8,g6) = 1.2
    c: Equal(g9,g10)
    c: Tangent(g10,g1)
    c: Tangent(g9,g1)
    c: Distance(g9,g10) = 1
    c: Tangent(g9,g7) = 1.5708
    c: Tangent(g8,g10) = 1.5708
    c: PointOnObject(g11,g1)
    c: Tangent(g10,g11) = 1.5708
    c: Tangent(g9,g11) = 1.5708
    c: Coincident(g12,g0)
    c: Diameter(g12) = 63.662
    c: Coincident(g5,g7)
    c: PointOnObject(g3,g12)
    c: Tangent(g8,g2)
    c: PointOnObject(g8,g4)
    c: PointOnObject(g5,g3)
    c: PointOnObject(g0,g3)
    c: Coincident(g5,g0)
    c: PointOnObject(g7,g3)
    c: Tangent(g7,g2)
    c: PointOnObject(g6,g2)
    c: PointOnObject(g6,g4)
    c: PointOnObject(g4,g12)
    c: PointOnObject(g4,g-1)
    c: Angle(g4,g3) = 0.15708
FEATURE [PartDesign::Pad] Pad015
  Direction = (0,0,1)
  Length = 16
  Length2 = 10
  Midplane = true
  Profile = -> Sketch048
  ReferenceAxis = -> Sketch048 [N_Axis]
  Type = 0
  expr: Length = Spreadsheet.mmPasWidth + Spreadsheet.mmPulleyConnectorThickness
FEATURE [PartDesign::PolarPattern] PolarPattern003
  Angle = 360
  Axis = -> Sketch048 [N_Axis]
  BaseFeature = -> Pad015
  Occurrences = 40
  Originals = -> [Pad015]
  expr: Angle = 360
  expr: Occurrences = Spreadsheet.cntPulleyTooth / 2 * 2
FEATURE [PartDesign::Body] Body012  label="PulleyOnRotorBody"
  Group = -> [Sketch048,Pad015,PolarPattern003]
  Origin = -> Origin023
  Tip = -> PolarPattern003
COMPONENT P6 — recipe-attached ("PulleyBorder", modeled in this document).
Construction recipe (the document's own serialized feature program — sketch geometry with constraints, then the solid features built on it; lengths are millimeters unless a unit is written):

FEATURE [Sketcher::SketchObject] Sketch049
  FullyConstrained = false
  MapMode = 5
  Placement = pos=(0,0,0) rot=(1,0,0;1.5708rad)
  Support = -> [XZ_Plane021]
  expr: Constraints[10] = Spreadsheet.mmAxisTubeDia / 2
  expr: Constraints[13] = Spreadsheet.mmPasWidth + Spreadsheet.mmPulleyConnectorThickness
  expr: Constraints[14] = Spreadsheet.mmPulleyConnectorThickness
  expr: Constraints[15] = Spreadsheet.mmPulleyConnectorHeight
  expr: Constraints[17] = Spreadsheet.mmPulleyConnectorThickness * 2
  expr: Constraints[21] = Spreadsheet.mmPulleyConnectorThickness / 3
  expr: Constraints[9] = Spreadsheet.mmPulleyExtDia / 2
  sketch-geometry (9):
    g0: LineSegment StartX=29.181 StartY=8 StartZ=0 EndX=20.4 EndY=8 EndZ=0
    g1: LineSegment StartX=20.4 StartY=8 StartZ=0 EndX=20.4 EndY=-32 EndZ=0
    g2: LineSegment StartX=20.4 StartY=-32 StartZ=0 EndX=24.4 EndY=-32 EndZ=0
    g3: LineSegment StartX=24.4 StartY=-32 StartZ=0 EndX=24.4 EndY=-16 EndZ=0
    g4: LineSegment StartX=24.4 StartY=-16 StartZ=0 EndX=31.0208 EndY=-9.37924 EndZ=0
    g5: LineSegment StartX=30.4955 StartY=-8.04591 StartZ=0 EndX=29.181 EndY=-8 EndZ=0
    g6: LineSegment StartX=29.181 StartY=-8 StartZ=0 EndX=29.181 EndY=8 EndZ=0
    g7: ArcOfCircle CenterX=29.4 CenterY=9.96836 CenterZ=0 NormalX=0 NormalY=0 NormalZ=1 AngleXU=0 Radius=1.7e-15 StartAngle=5.30264 EndAngle=9.80375
    g8: ArcOfCircle CenterX=30.4683 CenterY=-8.82676 CenterZ=0 NormalX=0 NormalY=0 NormalZ=1 AngleXU=0 Radius=0.781327 StartAngle=5.49779 EndAngle=7.81908
  constraints (22):
    c: Horizontal(g0)
    c: Coincident(g0,g1)
    c: Vertical(g1)
    c: Coincident(g1,g2)
    c: Coincident(g2,g3)
    c: Vertical(g3)
    c: Coincident(g3,g4)
    c: Coincident(g5,g6)
    c: Symmetric(g5,g6,g-1)
    c: DistanceX(g-1,g6) = 29.181
    c: DistanceX(g-1,g1) = 20.4
    c: Horizontal(g2)
    c: Angle(g-1,g4) = 0.785398
    c: DistanceY(g6,g6) = 16
    c: DistanceX(g2,g2) = 4
    c: DistanceY(g3,g3) = 16
    c: Angle(g-1,g5) = 3.10669
    c: DistanceY(g3,g5) = 8
    c: Coincident(g0,g6)
    c: Tangent(g5,g8) = -1.5708
    c: Tangent(g4,g8) = -1.5708
    c: DistanceY(g4,g5) = 1.33333
FEATURE [PartDesign::Revolution] Revolution005
  Angle = 360
  Axis = (0,-2e-16,1)
  Base = (0,0,0)
  Placement = pos=(0,0,0) rot=(1,0,0;1.5708rad)
  Profile = -> Sketch049
  ReferenceAxis = -> Sketch049 [V_Axis]
  expr: Angle = 360
FEATURE [Sketcher::SketchObject] Sketch050
  AttachmentOffset = pos=(0,0,-26) rot=(0,0,1;0rad)
  FullyConstrained = false
  MapMode = 5
  Placement = pos=(0,0,-26) rot=(0,0,1;0rad)
  Support = -> [XY_Plane021]
  expr: .AttachmentOffset.Base.z = -(Spreadsheet.mmPulleyConnectorHeight + Spreadsheet.mmPasWidth / 2 + Spreadsheet.mmPulleyConnectorThickness)
  expr: Constraints[10] = 360 / Spreadsheet.cntPulleyConnectorTooth / 4
  expr: Constraints[11] = Spreadsheet.mmAxisTubeDia + Spreadsheet.mmPulleyConnectorThickness - 2 * Spreadsheet.mmAirSpace
  expr: Constraints[14] = Spreadsheet.mmAirSpace / 2
  expr: Constraints[15] = Spreadsheet.mmAirSpace / 2
  expr: Constraints[23] = Spreadsheet.mmAxisTubeDia + Spreadsheet.mmPulleyConnectorThickness * 2 - Spreadsheet.mmAirSpace / 2
  expr: Constraints[2] = Spreadsheet.mmAxisTubeDia
  expr: Constraints[3] = Spreadsheet.mmAxisTubeDia + Spreadsheet.mmPulleyConnectorThickness * 2
  expr: Constraints[6] = 360 / Spreadsheet.cntPulleyConnectorTooth
  expr: Constraints[9] = 360 / Spreadsheet.cntPulleyConnectorTooth * 3 / 4
  sketch-geometry (14):
    g0: Circle CenterX=0 CenterY=0 CenterZ=0 NormalX=0 NormalY=0 NormalZ=1 AngleXU=0 Radius=20.4
    g1: Circle CenterX=0 CenterY=0 CenterZ=0 NormalX=0 NormalY=0 NormalZ=1 AngleXU=0 Radius=24.4
    g2: LineSegment StartX=0 StartY=0 StartZ=0 EndX=23.5686 EndY=6.31518 EndZ=0
    g3: LineSegment StartX=0 StartY=0 StartZ=0 EndX=23.9312 EndY=4.7602 EndZ=0
    g4: LineSegment StartX=0 StartY=0 StartZ=0 EndX=24.3478 EndY=1.59584 EndZ=0
    g5: ArcOfCircle CenterX=0 CenterY=0 CenterZ=0 NormalX=0 NormalY=0 NormalZ=1 AngleXU=0 Radius=21.6 StartAngle=0.0469303 EndAngle=0.214869
    g6: LineSegment StartX=21.1033 StartY=4.60554 StartZ=0 EndX=23.6537 EndY=5.11285 EndZ=0
    g7: LineSegment StartX=24.171 StartY=1.1834 StartZ=0 EndX=21.5762 EndY=1.01332 EndZ=0
    g8: ArcOfCircle CenterX=0 CenterY=0 CenterZ=0 NormalX=0 NormalY=0 NormalZ=1 AngleXU=0 Radius=24.4 StartAngle=1e-16 EndAngle=0.261799
    g9: ArcOfCircle CenterX=0 CenterY=0 CenterZ=0 NormalX=0 NormalY=0 NormalZ=1 AngleXU=0 Radius=24.2 StartAngle=0 EndAngle=0.0489202
    g10: LineSegment StartX=0 StartY=0 StartZ=0 EndX=30.359 EndY=0 EndZ=0
    g11: LineSegment StartX=24.2 StartY=0 StartZ=0 EndX=24.4 EndY=2.4e-15 EndZ=0
    g12: ArcOfCircle CenterX=0 CenterY=0 CenterZ=0 NormalX=0 NormalY=0 NormalZ=1 AngleXU=0 Radius=24.2 StartAngle=0.212879 EndAngle=0.261799
    g13: LineSegment StartX=23.3754 StartY=6.26342 StartZ=0 EndX=23.5686 EndY=6.31518 EndZ=0
  constraints (38):
    c: Coincident(g0,g-1)
    c: Coincident(g1,g0)
    c: Diameter(g0) = 40.8
    c: Diameter(g1) = 48.8
    c: Coincident(g2,g0)
    c: PointOnObject(g2,g1)
    c: Angle(g-1,g2) = 0.261799
    c: Coincident(g3,g0)
    c: Coincident(g4,g0)
    c: Angle(g-1,g3) = 0.19635
    c: Angle(g-1,g4) = 0.0654498
    c: Diameter(g5) = 43.2
    c: Parallel(g4,g7)
    c: Parallel(g6,g3)
    c: Distance(g6,g3) = 0.4
    c: Distance(g7,g4) = 0.4
    c: PointOnObject(g4,g1)
    c: PointOnObject(g3,g1)
    c: Coincident(g5,g6)
    c: Coincident(g5,g7)
    c: Coincident(g0,g5)
    c: Coincident(g8,g5)
    c: Coincident(g9,g5)
    c: Diameter(g9) = 48.4
    c: PointOnObject(g12,g2)
    c: Coincident(g10,g5)
    c: PointOnObject(g10,g-1)
    c: PointOnObject(g9,g10)
    c: Coincident(g11,g9)
    c: Parallel(g10,g11)
    c: Equal(g9,g12)
    c: Coincident(g9,g12)
    c: Coincident(g12,g6)
    c: Coincident(g9,g7)
    c: Coincident(g13,g12)
    c: Coincident(g13,g2)
    c: Coincident(g8,g13)
    c: Coincident(g11,g8)
FEATURE [PartDesign::Pocket] Pocket006
  BaseFeature = -> Revolution005
  Direction = (0,0,-1)
  Length = 16
  Length2 = 5
  Placement = pos=(0,0,0) rot=(1,0,0;1.5708rad)
  Profile = -> Sketch050
  ReferenceAxis = -> Sketch050 [N_Axis]
  Reversed = true
  Type = 0
  expr: Length = Spreadsheet.mmPulleyConnectorHeight
FEATURE [PartDesign::PolarPattern] PolarPattern004
  Angle = 360
  Axis = -> Sketch050 [N_Axis]
  BaseFeature = -> Pocket006
  Occurrences = 24
  Originals = -> [Pocket006]
  Placement = pos=(0,0,0) rot=(1,0,0;1.5708rad)
  expr: Angle = 360
  expr: Occurrences = Spreadsheet.cntPulleyConnectorTooth
FEATURE [PartDesign::Body] Body013  label="PulleyBorderBody"
  Group = -> [Sketch049,Revolution005,Sketch050,Pocket006,PolarPattern004]
  Origin = -> Origin025
  Tip = -> PolarPattern004
COMPONENT P7 — recipe-attached ("PulleyOnAxisFixator", modeled in this document).
Construction recipe (the document's own serialized feature program — sketch geometry with constraints, then the solid features built on it; lengths are millimeters unless a unit is written):

FEATURE [Sketcher::SketchObject] Sketch054
  FullyConstrained = true
  MapMode = 5
  Support = -> [XY_Plane025]
  expr: Constraints[2] = Spreadsheet.mmAxisTubeDia + Spreadsheet.mmPulleyConnectorThickness + Spreadsheet.mmAirSpace / 2
  expr: Constraints[3] = Spreadsheet.mmAxisTubeDia + Spreadsheet.mmPulleyConnectorThickness * 3
  sketch-geometry (2):
    g0: Circle CenterX=0 CenterY=0 CenterZ=0 NormalX=0 NormalY=0 NormalZ=1 AngleXU=0 Radius=22.6
    g1: Circle CenterX=0 CenterY=0 CenterZ=0 NormalX=0 NormalY=0 NormalZ=1 AngleXU=0 Radius=26.4
  constraints (4):
    c: Coincident(g0,g-1)
    c: Coincident(g1,g0)
    c: Diameter(g0) = 45.2
    c: Diameter(g1) = 52.8
FEATURE [PartDesign::Pad] Pad017
  Direction = (0,0,1)
  Length = 16
  Length2 = 10
  Profile = -> Sketch054
  ReferenceAxis = -> Sketch054 [N_Axis]
  Type = 0
  expr: Length = Spreadsheet.mmPulleyConnectorHeight
FEATURE [Sketcher::SketchObject] Sketch055
  FullyConstrained = false
  MapMode = 5
  Support = -> [XY_Plane025]
  expr: Constraints[16] = Spreadsheet.mmAxisTubeDia + Spreadsheet.mmPulleyConnectorThickness - Spreadsheet.mmAirSpace / 2
  expr: Constraints[2] = Spreadsheet.mmAxisTubeDia
  expr: Constraints[32] = 360 / Spreadsheet.cntPulleyConnectorTooth / 4
  expr: Constraints[33] = 360 / Spreadsheet.cntPulleyConnectorTooth / 4
  expr: Constraints[34] = 360 / Spreadsheet.cntPulleyConnectorTooth / 2
  expr: Constraints[3] = Spreadsheet.mmAxisTubeDia + Spreadsheet.mmPulleyConnectorThickness * 2
  expr: Constraints[6] = Spreadsheet.mmAxisTubeDia + Spreadsheet.mmPulleyConnectorThickness
  sketch-geometry (15):
    g0: Circle CenterX=0 CenterY=0 CenterZ=0 NormalX=0 NormalY=0 NormalZ=1 AngleXU=0 Radius=20.4
    g1: Circle CenterX=0 CenterY=0 CenterZ=0 NormalX=0 NormalY=0 NormalZ=1 AngleXU=0 Radius=24.4
    g2: LineSegment StartX=0 StartY=0 StartZ=0 EndX=25.9633 EndY=3.41813 EndZ=0
    g3: LineSegment StartX=0 StartY=0 StartZ=0 EndX=24.7789 EndY=-3.2622 EndZ=0
    g4: ArcOfCircle CenterX=0 CenterY=0 CenterZ=0 NormalX=0 NormalY=0 NormalZ=1 AngleXU=0 Radius=22.4 StartAngle=6.15229 EndAngle=6.21774
    g5: LineSegment StartX=22.2084 StartY=2.92379 StartZ=0 EndX=22.0101 EndY=2.89768 EndZ=0
    g6: LineSegment StartX=22.0101 StartY=-2.89768 StartZ=0 EndX=22.2084 EndY=-2.92379 EndZ=0
    g7: ArcOfCircle CenterX=0 CenterY=0 CenterZ=0 NormalX=0 NormalY=0 NormalZ=1 AngleXU=0 Radius=22.2 StartAngle=6.15229 EndAngle=6.41409
    g8: LineSegment StartX=0 StartY=0 StartZ=0 EndX=26.0465 EndY=-1.70718 EndZ=0
    g9: LineSegment StartX=0 StartY=0 StartZ=0 EndX=26.0465 EndY=1.70718 EndZ=0
    g10: Circle CenterX=0 CenterY=0 CenterZ=0 NormalX=0 NormalY=0 NormalZ=1 AngleXU=0 Radius=22.2
    g11: ArcOfCircle CenterX=0 CenterY=0 CenterZ=0 NormalX=0 NormalY=0 NormalZ=1 AngleXU=0 Radius=22.4 StartAngle=0.0654498 EndAngle=0.1309
    g12: LineSegment StartX=22.352 StartY=1.46503 StartZ=0 EndX=24.3478 EndY=1.59584 EndZ=0
    g13: ArcOfCircle CenterX=0 CenterY=0 CenterZ=0 NormalX=0 NormalY=0 NormalZ=1 AngleXU=0 Radius=24.4 StartAngle=6.21774 EndAngle=6.34864
    g14: LineSegment StartX=22.352 StartY=-1.46503 StartZ=0 EndX=24.3478 EndY=-1.59584 EndZ=0
  constraints (38):
    c: Coincident(g0,g-1)
    c: Coincident(g1,g0)
    c: Diameter(g0) = 40.8
    c: Diameter(g1) = 48.8
    c: Coincident(g2,g0)
    c: Coincident(g3,g0)
    c: Diameter(g4) = 44.8
    c: Parallel(g3,g6)
    c: Parallel(g5,g2)
    c: Coincident(g11,g5)
    c: Coincident(g4,g6)
    c: Coincident(g0,g4)
    c: Coincident(g7,g4)
    c: Coincident(g8,g4)
    c: Coincident(g9,g4)
    c: Coincident(g10,g4)
    c: Diameter(g10) = 44.4
    c: Equal(g4,g11)
    c: PointOnObject(g4,g8)
    c: PointOnObject(g11,g9)
    c: Coincident(g4,g11)
    c: Coincident(g12,g11)
    c: PointOnObject(g5,g10)
    c: PointOnObject(g12,g1)
    c: Coincident(g14,g4)
    c: Parallel(g9,g12)
    c: PointOnObject(g5,g2)
    c: PointOnObject(g4,g3)
    c: Coincident(g13,g12)
    c: Coincident(g14,g13)
    c: Coincident(g7,g5)
    c: Coincident(g6,g7)
    c: Angle(g9,g2) = 0.0654498
    c: Angle(g3,g8) = 0.0654498
    c: Angle(g8,g9) = 0.1309
    c: Symmetric(g8,g9,g-1)
    c: Coincident(g4,g13)
    c: PointOnObject(g13,g8)
FEATURE [PartDesign::Pocket] Pocket009
  BaseFeature = -> Pad017
  Direction = (0,0,-1)
  Length = 16
  Length2 = 5
  Profile = -> Sketch055
  ReferenceAxis = -> Sketch055 [N_Axis]
  Reversed = true
  Type = 0
  expr: Length = Spreadsheet.mmPulleyConnectorHeight
FEATURE [PartDesign::PolarPattern] PolarPattern005
  Angle = 360
  Axis = -> Sketch055 [N_Axis]
  BaseFeature = -> Pocket009
  Occurrences = 24
  Originals = -> [Pocket009]
  expr: Occurrences = Spreadsheet.cntPulleyConnectorTooth
FEATURE [Sketcher::SketchObject] Sketch056
  FullyConstrained = true
  MapMode = 5
  Support = -> [XY_Plane025]
  expr: Constraints[2] = Spreadsheet.mmAxisTubeDia
  expr: Constraints[3] = Spreadsheet.mmAxisTubeDia + Spreadsheet.mmPetalHightMax * 4
  sketch-geometry (2):
    g0: Circle CenterX=0 CenterY=0 CenterZ=0 NormalX=0 NormalY=0 NormalZ=1 AngleXU=0 Radius=20.4
    g1: Circle CenterX=0 CenterY=0 CenterZ=0 NormalX=0 NormalY=0 NormalZ=1 AngleXU=0 Radius=32.64
  constraints (4):
    c: Coincident(g0,g-1)
    c: Coincident(g1,g0)
    c: Diameter(g0) = 40.8
    c: Diameter(g1) = 65.28
FEATURE [PartDesign::Pad] Pad018
  BaseFeature = -> PolarPattern005
  Direction = (0,0,1)
  Length = 20.4
  Length2 = 10
  Profile = -> Sketch056
  ReferenceAxis = -> Sketch056 [N_Axis]
  Reversed = true
  Type = 0
  expr: Length = Spreadsheet.mmAxisTubeDia / 2
FEATURE [Sketcher::SketchObject] Sketch057  label="PulleyPetalPocketMaxSketch"
  AttachmentOffset = pos=(0,0,-20.4) rot=(0,0,1;0rad)
  FullyConstrained = true
  MapMode = 5
  Placement = pos=(0,0,-20.4) rot=(0,0,1;0rad)
  Support = -> [XY_Plane025]
  expr: .AttachmentOffset.Base.z = -(Spreadsheet.mmAxisTubeDia / 2)
  expr: Constraints[1] = Spreadsheet.mmAxisTubeDia
  expr: Constraints[7] = Spreadsheet.mmPetalPocketWidth
  expr: Constraints[8] = Spreadsheet.mmAxisTubeDia / 2 + Spreadsheet.mmPetalHightMax
  sketch-geometry (4):
    g0: ArcOfCircle CenterX=0 CenterY=0 CenterZ=0 NormalX=0 NormalY=0 NormalZ=1 AngleXU=0 Radius=20.4 StartAngle=6.00103 EndAngle=6.56534
    g1: LineSegment StartX=19.5933 StartY=5.67991 StartZ=0 EndX=26.52 EndY=5.67991 EndZ=0
    g2: LineSegment StartX=26.52 StartY=5.67991 StartZ=0 EndX=26.52 EndY=-5.67991 EndZ=0
    g3: LineSegment StartX=26.52 StartY=-5.67991 StartZ=0 EndX=19.5933 EndY=-5.67991 EndZ=0
  constraints (11):
    c: Coincident(g0,g-1)
    c: Diameter(g0) = 40.8
    c: Horizontal(g1)
    c: Coincident(g1,g2)
    c: Coincident(g2,g3)
    c: Horizontal(g3)
    c: Symmetric(g1,g2,g-1)
    c: DistanceY(g2,g2) = 11.3598
    c: DistanceX(g0,g2) = 26.52
    c: Coincident(g0,g1)
    c: Coincident(g0,g3)
FEATURE [Sketcher::SketchObject] Sketch058  label="PulleyPetalPocketMinSketch"
  AttachmentOffset = pos=(0,0,-2.04) rot=(0,0,1;0rad)
  FullyConstrained = true
  MapMode = 5
  Placement = pos=(0,0,-2.04) rot=(0,0,1;0rad)
  Support = -> [XY_Plane025]
  expr: .AttachmentOffset.Base.z = -(Spreadsheet.mmAxisTubeDia / 2 - Spreadsheet.mmFixatorHight * 0.9)
  expr: Constraints[1] = Spreadsheet.mmAxisTubeDia
  expr: Constraints[7] = Spreadsheet.mmAxisTubeDia / 2 + Spreadsheet.mmPetalHightMin
  expr: Constraints[8] = Spreadsheet.mmPetalPocketWidth
  sketch-geometry (4):
    g0: ArcOfCircle CenterX=0 CenterY=0 CenterZ=0 NormalX=0 NormalY=0 NormalZ=1 AngleXU=0 Radius=20.4 StartAngle=6.00103 EndAngle=6.56534
    g1: LineSegment StartX=19.5933 StartY=5.67991 StartZ=0 EndX=23.46 EndY=5.67991 EndZ=0
    g2: LineSegment StartX=23.46 StartY=5.67991 StartZ=0 EndX=23.46 EndY=-5.67991 EndZ=0
    g3: LineSegment StartX=23.46 StartY=-5.67991 StartZ=0 EndX=19.5933 EndY=-5.67991 EndZ=0
  constraints (11):
    c: Coincident(g0,g-1)
    c: Diameter(g0) = 40.8
    c: Horizontal(g1)
    c: Coincident(g1,g2)
    c: Coincident(g2,g3)
    c: Symmetric(g1,g2,g-1)
    c: Horizontal(g3)
    c: DistanceX(g0,g2) = 23.46
    c: DistanceY(g2,g2) = 11.3598
    c: Coincident(g0,g1)
    c: Coincident(g0,g3)
FEATURE [PartDesign::SubtractiveLoft] SubtractiveLoft003
  BaseFeature = -> Pad018
  Closed = false
  Profile = -> Sketch057
  Ruled = false
  Sections = -> [Sketch058]
FEATURE [PartDesign::PolarPattern] PolarPattern006
  Angle = 360
  Axis = -> Sketch057 [N_Axis]
  BaseFeature = -> SubtractiveLoft003
  Occurrences = 3
  Originals = -> [SubtractiveLoft003]
FEATURE [PartDesign::Chamfer] Chamfer009
  Angle = 45
  Base = -> PolarPattern006 [Edge2]
  BaseFeature = -> PolarPattern006
  ChamferType = 1
  FlipDirection = false
  Size = 1
  Size2 = 3
  SupportTransform = false
  UseAllEdges = false
FEATURE [Sketcher::SketchObject] Sketch060
  FullyConstrained = true
  MapMode = 5
  Placement = pos=(0,0,0) rot=(1,0,0;1.5708rad)
  Support = -> [XZ_Plane025]
  expr: Constraints[11] = Spreadsheet.mmPulleyIntDia / 2
  expr: Constraints[13] = (Spreadsheet.mmAxisTubeDia + Spreadsheet.mmPetalHightMax * 4) / 2
  expr: Constraints[7] = Spreadsheet.mmPulleyConnectorThickness / 3
  expr: Constraints[8] = Spreadsheet.mmPulleyConnectorThickness * 2
  sketch-geometry (5):
    g0: LineSegment StartX=26.4 StartY=0 StartZ=0 EndX=26.4 EndY=-8 EndZ=0
    g1: LineSegment StartX=26.4 StartY=-8 StartZ=0 EndX=32.64 EndY=-8 EndZ=0
    g2: LineSegment StartX=32.64 StartY=-8 StartZ=0 EndX=39.3067 EndY=-1.33333 EndZ=0
    g3: LineSegment StartX=38.7544 StartY=0 StartZ=0 EndX=26.4 EndY=0 EndZ=0
    g4: ArcOfCircle CenterX=38.7544 CenterY=-0.781049 CenterZ=0 NormalX=0 NormalY=0 NormalZ=1 AngleXU=0 Radius=0.781049 StartAngle=5.49779 EndAngle=7.85398
  constraints (14):
    c: Coincident(g0,g1)
    c: Horizontal(g1)
    c: Coincident(g1,g2)
    c: Coincident(g3,g0)
    c: Horizontal(g3)
    c: Tangent(g3,g4) = -1.5708
    c: Tangent(g2,g4) = -1.5708
    c: DistanceY(g2,g3) = 1.33333
    c: DistanceY(g0,g0) = 8
    c: PointOnObject(g0,g-1)
    c: Angle(g-1,g2) = 0.785398
    c: DistanceX(g-1,g0) = 26.4
    c: Vertical(g0)
    c: DistanceX(g-1,g1) = 32.64
FEATURE [PartDesign::Revolution] Revolution007
  Angle = 360
  Axis = (0,-2e-16,1)
  Base = (0,0,0)
  BaseFeature = -> Chamfer009
  Profile = -> Sketch060
  ReferenceAxis = -> Sketch060 [V_Axis]
  Reversed = true
FEATURE [PartDesign::Body] Body015  label="PulleyOnAxisFixatorBody"
  Group = -> [Sketch054,Pad017,Sketch055,Pocket009,PolarPattern005,Sketch056,Pad018,Sketch057,Sketch058,SubtractiveLoft003,PolarPattern006,Chamfer009,Sketch060,Revolution007]
  Origin = -> Origin029
  Tip = -> Revolution007
COMPONENT P8 — recipe-attached ("PulleyUpSeparatorPart", modeled in this document).
Construction recipe (the document's own serialized feature program — sketch geometry with constraints, then the solid features built on it; lengths are millimeters unless a unit is written):

FEATURE [Sketcher::SketchObject] Sketch059
  FullyConstrained = true
  MapMode = 5
  Placement = pos=(0,0,0) rot=(1,0,0;1.5708rad)
  Support = -> [XZ_Plane028]
  expr: Constraints[10] = Spreadsheet.mmPulleyConnectorThickness
  expr: Constraints[11] = Spreadsheet.mmPulleyConnectorThickness / 3
  expr: Constraints[12] = Spreadsheet.mmPulleyIntDia / 2
  expr: Constraints[13] = Spreadsheet.mmPulleyExtDia / 2
  sketch-geometry (6):
    g0: LineSegment StartX=26.4 StartY=2 StartZ=0 EndX=26.4 EndY=-2 EndZ=0
    g1: LineSegment StartX=26.4 StartY=-2 StartZ=0 EndX=29.181 EndY=-2 EndZ=0
    g2: LineSegment StartX=29.181 StartY=-2 StartZ=0 EndX=31.8477 EndY=0.666667 EndZ=0
    g3: LineSegment StartX=31.2954 StartY=2 StartZ=0 EndX=29.181 EndY=2 EndZ=0
    g4: LineSegment StartX=29.181 StartY=2 StartZ=0 EndX=26.4 EndY=2 EndZ=0
    g5: ArcOfCircle CenterX=31.2954 CenterY=1.21895 CenterZ=0 NormalX=0 NormalY=0 NormalZ=1 AngleXU=0 Radius=0.781049 StartAngle=5.49779 EndAngle=7.85398
  constraints (16):
    c: Coincident(g0,g1)
    c: Horizontal(g1)
    c: Coincident(g1,g2)
    c: Coincident(g3,g4)
    c: Coincident(g4,g0)
    c: Horizontal(g4)
    c: Symmetric(g0,g0,g-1)
    c: Equal(g1,g4)
    c: Tangent(g3,g5) = -1.5708
    c: Tangent(g2,g5) = -1.5708
    c: DistanceY(g0,g0) = 4
    c: DistanceY(g2,g3) = 1.33333
    c: DistanceX(g-1,g0) = 26.4
    c: DistanceX(g-1,g3) = 29.181
    c: Angle(g-1,g2) = 0.785398
    c: Horizontal(g3)
FEATURE [PartDesign::Revolution] Revolution006
  Angle = 360
  Axis = (0,2e-16,1)
  Base = (0,0,0)
  Placement = pos=(0,0,0) rot=(1,0,0;1.5708rad)
  Profile = -> Sketch059
  ReferenceAxis = -> Sketch059 [V_Axis]
  Reversed = true
FEATURE [PartDesign::Body] Body016  label="PulleySeparatorBody"
  Group = -> [Sketch059,Revolution006]
  Origin = -> Origin032
  Tip = -> Revolution006
COMPONENT P9 — recipe-attached ("PetalPart", modeled in this document).
Construction recipe (the document's own serialized feature program — sketch geometry with constraints, then the solid features built on it; lengths are millimeters unless a unit is written):

FEATURE [Sketcher::SketchObject] Sketch029  label="MaxPetalBase"
  FullyConstrained = false
  MapMode = 5
  Placement = pos=(0,0,0) rot=(0.57735,0.57735,0.57735;2.0944rad)
  Support = -> [YZ_Plane015]
  expr: Constraints[0] = Spreadsheet.mmAxisTubeDia + 2 * Spreadsheet.mmFixatorThick
  expr: Constraints[12] = Spreadsheet.mmAxisTubeDia / 2 + Spreadsheet.mmPetalHightMax
  expr: Constraints[16] = Spreadsheet.mmPetalWidth
  expr: Constraints[1] = Spreadsheet.mmAxisTubeDia
  expr: Constraints[6] = Spreadsheet.mmAxisTubeDia + Spreadsheet.mmTwoSideTapeThick * 2
  sketch-geometry (7):
    g0: Circle CenterX=0 CenterY=0 CenterZ=0 NormalX=0 NormalY=0 NormalZ=1 AngleXU=0 Radius=39.8652
    g1: Circle CenterX=0 CenterY=0 CenterZ=0 NormalX=0 NormalY=0 NormalZ=1 AngleXU=0 Radius=26.62
    g2: ArcOfCircle CenterX=0 CenterY=0 CenterZ=0 NormalX=0 NormalY=0 NormalZ=1 AngleXU=0 Radius=20.4 StartAngle=3.89684 EndAngle=6.80091
    g3: LineSegment StartX=19.8084 StartY=5.27991 StartZ=0 EndX=26.52 EndY=5.27991 EndZ=0
    g4: LineSegment StartX=26.52 StartY=5.27991 StartZ=0 EndX=26.52 EndY=-5.27991 EndZ=0
    g5: LineSegment StartX=26.52 StartY=-5.27991 StartZ=0 EndX=19.8084 EndY=-5.27991 EndZ=0
    g6: ArcOfCircle CenterX=0 CenterY=0 CenterZ=0 NormalX=0 NormalY=0 NormalZ=1 AngleXU=0 Radius=20.5 StartAngle=6.02269 EndAngle=6.54368
  constraints (20):
    c: Diameter(g1) = 53.24
    c: Diameter(g2) = 40.8
    c: Coincident(g3,g4)
    c: Coincident(g4,g5)
    c: PointOnObject(g3,g2)
    c: Coincident(g6,g0)
    c: Diameter(g6) = 41
    c: Coincident(g1,g6)
    c: Coincident(g0,g2)
    c: Vertical(g4)
    c: PointOnObject(g3,g6)
    c: PointOnObject(g5,g6)
    c: DistanceX(g-1,g4) = 26.52
    c: Horizontal(g3)
    c: Horizontal(g5)
    c: Symmetric(g5,g3,g-1)
    c: DistanceY(g5,g3) = 10.5598
    c: Coincident(g-1,g6)
    c: PointOnObject(g6,g5)
    c: PointOnObject(g6,g3)
FEATURE [Sketcher::SketchObject] Sketch030  label="MinPetalBase"
  AttachmentOffset = pos=(0,0,20.4) rot=(0,0,1;0rad)
  FullyConstrained = false
  MapMode = 5
  Placement = pos=(20.4,-4.5e-15,4.5e-15) rot=(0.57735,0.57735,0.57735;2.0944rad)
  Support = -> [YZ_Plane015]
  expr: .AttachmentOffset.Base.z = Spreadsheet.mmFixatorHight
  expr: Constraints[0] = Spreadsheet.mmAxisTubeDia + 2 * Spreadsheet.mmFixatorThick
  expr: Constraints[11] = Spreadsheet.mmAxisTubeDia / 2 + Spreadsheet.mmPetalHightMin
  expr: Constraints[15] = Spreadsheet.mmPetalWidth
  expr: Constraints[1] = Spreadsheet.mmAxisTubeDia
  expr: Constraints[5] = Spreadsheet.mmAxisTubeDia + Spreadsheet.mmTwoSideTapeThick * 2
  sketch-geometry (7):
    g0: Circle CenterX=0 CenterY=1.8e-15 CenterZ=0 NormalX=0 NormalY=0 NormalZ=1 AngleXU=0 Radius=39.865
    g1: Circle CenterX=0 CenterY=1.8e-15 CenterZ=0 NormalX=0 NormalY=0 NormalZ=1 AngleXU=0 Radius=26.62
    g2: ArcOfCircle CenterX=0 CenterY=1.8e-15 CenterZ=0 NormalX=0 NormalY=0 NormalZ=1 AngleXU=0 Radius=20.4 StartAngle=3.86544 EndAngle=6.7404
    g3: LineSegment StartX=19.8084 StartY=5.27991 StartZ=0 EndX=23.46 EndY=5.27991 EndZ=0
    g4: LineSegment StartX=23.46 StartY=5.27991 StartZ=0 EndX=23.46 EndY=-5.27991 EndZ=0
    g5: LineSegment StartX=23.46 StartY=-5.27991 StartZ=0 EndX=19.8084 EndY=-5.27991 EndZ=0
    g6: ArcOfCircle CenterX=0 CenterY=1.8e-15 CenterZ=0 NormalX=0 NormalY=0 NormalZ=1 AngleXU=0 Radius=20.5 StartAngle=6.02269 EndAngle=6.54368
  constraints (20):
    c: Diameter(g1) = 53.24
    c: Diameter(g2) = 40.8
    c: Coincident(g3,g4)
    c: Coincident(g4,g5)
    c: Coincident(g6,g0)
    c: Diameter(g6) = 41
    c: Coincident(g1,g6)
    c: Coincident(g0,g2)
    c: Vertical(g4)
    c: PointOnObject(g3,g6)
    c: PointOnObject(g5,g6)
    c: DistanceX(g-1,g4) = 23.46
    c: PointOnObject(g6,g5)
    c: PointOnObject(g6,g3)
    c: Coincident(g6,g-1)
    c: DistanceY(g5,g3) = 10.5598
    c: Symmetric(g5,g3,g-1)
    c: Horizontal(g3)
    c: Horizontal(g5)
    c: PointOnObject(g6,g-2)
FEATURE [PartDesign::AdditiveLoft] AdditiveLoft  label="PetalBodyBodyAdditiveLoft"
  Closed = false
  Placement = pos=(0,0,0) rot=(1,1,1;2.0944rad)
  Profile = -> Sketch029
  Ruled = false
  Sections = -> [Sketch030]
FEATURE [PartDesign::Chamfer] Chamfer
  Angle = 45
  Base = -> AdditiveLoft [Edge8,Edge9,Edge6,Edge3,Edge2,Edge1,Edge11,Edge5]
  BaseFeature = -> AdditiveLoft
  ChamferType = 0
  FlipDirection = false
  Placement = pos=(0,0,0) rot=(1,1,1;2.0944rad)
  Size = 1
  Size2 = 1
  SupportTransform = false
  UseAllEdges = false
FEATURE [PartDesign::Body] Body008  label="PetalBodyPart"
  Group = -> [Sketch029,Sketch030,AdditiveLoft,Chamfer]
  Origin = -> Origin015
  Tip = -> Chamfer
PROVENANCE & LICENSES
A FreeCAD (.FCStd) document from a public repository crawl; recipes are the document's own serialized feature recipes (and, for linked parts, companion documents' recipes).
License: as declared in the source repository (recorded in the dataset sidecar).
